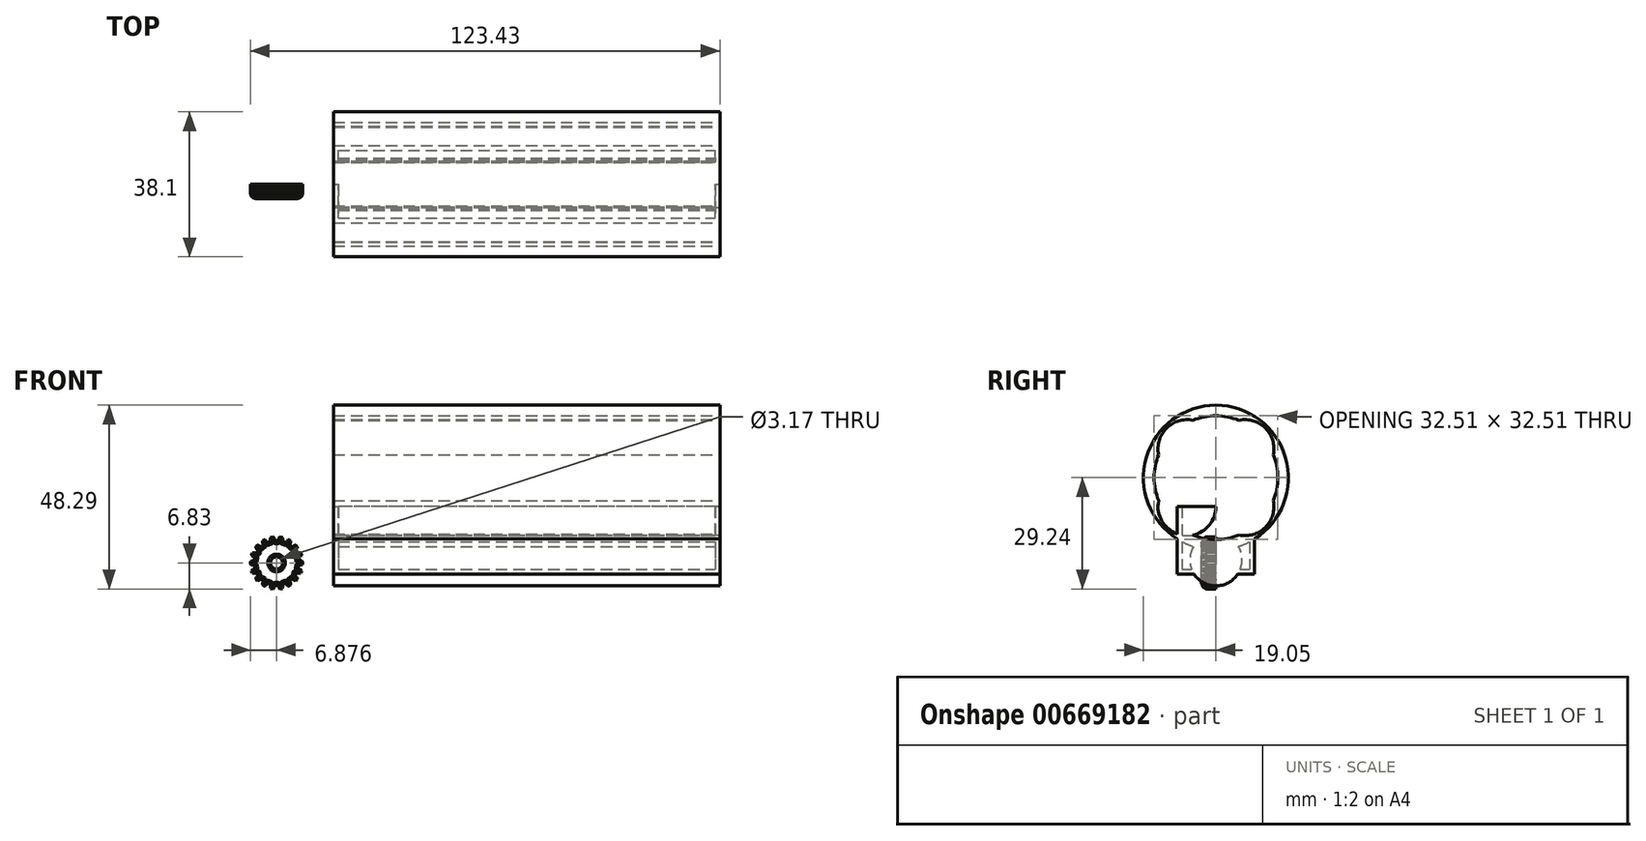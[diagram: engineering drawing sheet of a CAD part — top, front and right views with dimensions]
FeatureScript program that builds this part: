
annotation { "Feature Type Name" : "Feature", "Feature Type Description" : "" }
export const myFeature = defineFeature(function(context is Context, id is Id, definition is map)
    precondition{}
    {
        {
            var Q0;
            Q0=qCreatedBy(makeId("Top.planeOp"),FACE);
            var sketch = newSketch(context, id + "F0", { "sketchPlane" : qUnion([Q0])});
            skLineSegment(sketch, "E0.bottom", {"start": v(50.8, 10.16) * mm, "end": v(-50.8, 10.16) * mm});
            skLineSegment(sketch, "E0.top", {"start": v(50.8, -10.16) * mm, "end": v(-50.8, -10.16) * mm});
            skLineSegment(sketch, "E0.left", {"start": v(50.8, 10.16) * mm, "end": v(50.8, -10.16) * mm});
            skLineSegment(sketch, "E0.right", {"start": v(-50.8, 10.16) * mm, "end": v(-50.8, -10.16) * mm});
            skPoint(sketch, "E0.middle", {"position": v(0, 0) * mm});
            skLineSegment(sketch, "E1.0", {"start": v(49.53, 8.9) * mm, "end": v(-49.53, 8.9) * mm});
            skLineSegment(sketch, "E1.1", {"start": v(49.53, 8.9) * mm, "end": v(49.53, -8.9) * mm});
            skLineSegment(sketch, "E1.2", {"start": v(49.53, -8.9) * mm, "end": v(-49.53, -8.9) * mm});
            skLineSegment(sketch, "E1.3", {"start": v(-49.53, 8.9) * mm, "end": v(-49.53, -8.9) * mm});
            skSolve(sketch);
        }
        {
            var Q0;
            Q0=makeQuery(id+"F0.imprint","IMPRINT",FACE,{"disambiguationData":[TD([[makeQuery(id+"F0.imprint","IMPRINT",EDGE,{"derivedFrom":sQuery(id+"F0.wireOp",EDGE,"E1.0")}),1.0]])]});
            var Q1;
            Q1=makeQuery(id+"F0.imprint","IMPRINT",FACE,{"disambiguationData":[TD([[makeQuery(id+"F0.imprint","IMPRINT",EDGE,{"derivedFrom":sQuery(id+"F0.wireOp",EDGE,"E0.bottom")}),1.0]])]});
            extrude(context, id + "F1", {"entities" : qUnion([Q0, Q1]), "depth" : 1.27 * mm, "offsetDistance" : 25.4 * mm});
        }
        {
            var Q0;
            Q0=makeQuery(id+"F0.imprint","IMPRINT",FACE,{"disambiguationData":[TD([[makeQuery(id+"F0.imprint","IMPRINT",EDGE,{"derivedFrom":sQuery(id+"F0.wireOp",EDGE,"E0.bottom")}),1.0]])]});
            extrude(context, id + "F2", {"entities" : qUnion([Q0]), "operationType" : NewBodyOperationType.ADD, "depth" : 17.78 * mm, "offsetDistance" : 25.4 * mm});
        }
        {
            var Q0;
            {var subQ0=sQuery(id+"F0.wireOp",EDGE,"E0.top");Q0=makeQuery(id+"F2.boolean.opBoolean","MERGE",FACE,{"derivedFrom":[makeQuery(id+"F1.opExtrude","SWEPT_FACE",FACE,{"disambiguationData":[OSD([subQ0])]}),makeQuery(id+"F2.opExtrude","SWEPT_FACE",FACE,{"disambiguationData":[OSD([subQ0])]})]});}
            var sketch = newSketch(context, id + "F3", { "sketchPlane" : qUnion([Q0])});
            skCircle(sketch, "E2", {"center": v(35.56, 3.81) * mm, "radius": 12.7 * mm});
            skLineSegment(sketch, "E3", {"start": v(0, 1.21) * mm, "end": v(0, 17.78) * mm, "construction": true});
            skCircle(sketch, "E4.MirrorC", {"center": v(-35.56, 3.81) * mm, "radius": 12.7 * mm});
            skSolve(sketch);
        }
        {
            var Q0;
            {var subQ0=sQuery(id+"F0.wireOp",EDGE,"E0.left");Q0=makeQuery(id+"F2.boolean.opBoolean","MERGE",FACE,{"derivedFrom":[makeQuery(id+"F1.opExtrude","SWEPT_FACE",FACE,{"disambiguationData":[OSD([subQ0])]}),makeQuery(id+"F2.opExtrude","SWEPT_FACE",FACE,{"disambiguationData":[OSD([subQ0])]})]});}
            var sketch = newSketch(context, id + "F4", { "sketchPlane" : qUnion([Q0])});
            skCircle(sketch, "E5", {"center": v(0, 25.4) * mm, "radius": 19.05 * mm});
            skPoint(sketch, "E5.centerSnap0", {"position": v(0, 0) * mm});
            skPoint(sketch, "E6", {"position": v(0, 17.78) * mm});
            skCircle(sketch, "E7", {"center": v(-7.62, 33.02) * mm, "radius": 7.62 * mm});
            skCircle(sketch, "E8", {"center": v(7.62, 33.02) * mm, "radius": 7.62 * mm});
            skCircle(sketch, "E9", {"center": v(7.62, 17.78) * mm, "radius": 7.62 * mm});
            skCircle(sketch, "E10", {"center": v(-7.62, 17.78) * mm, "radius": 7.62 * mm});
            skLineSegment(sketch, "E11", {"start": v(-7.62, 33.02) * mm, "end": v(7.62, 17.78) * mm, "construction": true});
            skLineSegment(sketch, "E12", {"start": v(7.62, 33.02) * mm, "end": v(-7.62, 17.78) * mm, "construction": true});
            skPoint(sketch, "E13.0", {"position": v(-10.16, 3.81) * mm});
            skCircle(sketch, "E14", {"center": v(0, 3.81) * mm, "radius": 6.86 * mm});
            skCircle(sketch, "E15", {"center": v(0, 25.4) * mm, "radius": 16.26 * mm});
            skSolve(sketch);
        }
        {
            var Q0;
            Q0 = qSketchRegion(id + "F4", true);
            extrude(context, id + "F5", {"entities" : qUnion([Q0]), "operationType" : NewBodyOperationType.ADD, "oppositeDirection" : true, "depth" : 101.6 * mm, "offsetDistance" : 25.4 * mm});
        }
        {
            var Q0;
            {var subQ0=sQuery(id+"F4.wireOp",EDGE,"E15");var subQ1=sQuery(id+"F4.wireOp",EDGE,"E9");var subQ2=makeQuery(id+"F4.imprint","INTERSECT",VERTEX,{"disambiguationData":[OD(1.0)],"derivedFrom":[subQ1,subQ0]});Q0=makeQuery(id+"F4.imprint","IMPRINT",FACE,{"disambiguationData":[TD([[makeQuery(id+"F4.imprint","IMPRINT",EDGE,{"disambiguationData":[TD([[subQ2,1.0]])],"derivedFrom":subQ1}),1.0]])]});}
            var Q1;
            {var subQ0=sQuery(id+"F4.wireOp",EDGE,"E15");var subQ1=sQuery(id+"F4.wireOp",EDGE,"E14");var subQ2=makeQuery(id+"F4.imprint","INTERSECT",VERTEX,{"disambiguationData":[OD(0.0)],"derivedFrom":[subQ1,subQ0]});Q1=makeQuery(id+"F4.imprint","IMPRINT",FACE,{"disambiguationData":[TD([[makeQuery(id+"F4.imprint","IMPRINT",EDGE,{"disambiguationData":[TD([[subQ2,-1.0]])],"derivedFrom":subQ1}),1.0]])]});}
            var Q2;
            {var subQ0=sQuery(id+"F4.wireOp",EDGE,"E15");var subQ1=sQuery(id+"F4.wireOp",EDGE,"E14");var subQ2=makeQuery(id+"F4.imprint","INTERSECT",VERTEX,{"disambiguationData":[OD(0.0)],"derivedFrom":[subQ1,subQ0]});Q2=makeQuery(id+"F4.imprint","IMPRINT",FACE,{"disambiguationData":[TD([[makeQuery(id+"F4.imprint","IMPRINT",EDGE,{"disambiguationData":[TD([[subQ2,-1.0]])],"derivedFrom":subQ1}),-1.0]])]});}
            var Q3;
            {var subQ0=sQuery(id+"F4.wireOp",EDGE,"E15");var subQ1=sQuery(id+"F4.wireOp",EDGE,"E10");var subQ2=makeQuery(id+"F4.imprint","INTERSECT",VERTEX,{"disambiguationData":[OD(1.0)],"derivedFrom":[subQ1,subQ0]});Q3=makeQuery(id+"F4.imprint","IMPRINT",FACE,{"disambiguationData":[TD([[makeQuery(id+"F4.imprint","IMPRINT",EDGE,{"disambiguationData":[TD([[subQ2,-1.0]])],"derivedFrom":subQ1}),1.0]])]});}
            var Q4;
            {var subQ0=sQuery(id+"F4.wireOp",EDGE,"E15");var subQ1=sQuery(id+"F4.wireOp",EDGE,"E9");var subQ2=makeQuery(id+"F4.imprint","INTERSECT",VERTEX,{"disambiguationData":[OD(1.0)],"derivedFrom":[subQ1,subQ0]});Q4=makeQuery(id+"F4.imprint","IMPRINT",FACE,{"disambiguationData":[TD([[makeQuery(id+"F4.imprint","IMPRINT",EDGE,{"disambiguationData":[TD([[subQ2,-1.0]])],"derivedFrom":subQ1}),1.0]])]});}
            var Q5;
            {var subQ0=sQuery(id+"F4.wireOp",EDGE,"E15");var subQ1=sQuery(id+"F4.wireOp",EDGE,"E10");var subQ2=makeQuery(id+"F4.imprint","INTERSECT",VERTEX,{"disambiguationData":[OD(1.0)],"derivedFrom":[subQ1,subQ0]});Q5=makeQuery(id+"F4.imprint","IMPRINT",FACE,{"disambiguationData":[TD([[makeQuery(id+"F4.imprint","IMPRINT",EDGE,{"disambiguationData":[TD([[subQ2,1.0]])],"derivedFrom":subQ1}),1.0]])]});}
            extrude(context, id + "F6", {"entities" : qUnion([Q0, Q1, Q2, Q3, Q4, Q5]), "operationType" : NewBodyOperationType.REMOVE, "oppositeDirection" : true, "depth" : 101.6 * mm, "offsetDistance" : 25.4 * mm});
        }
        {
            var Q0;
            Q0=qCreatedBy(makeId("Front.planeOp"),FACE);
            var sketch = newSketch(context, id + "F7", { "sketchPlane" : qUnion([Q0])});
            skLineSegment(sketch, "E16", {"start": v(-59.99, 3.75) * mm, "end": v(-59.95, 3.68) * mm});
            skLineSegment(sketch, "E17", {"start": v(-59.95, 3.68) * mm, "end": v(-59.92, 3.66) * mm});
            skLineSegment(sketch, "E18", {"start": v(-59.92, 3.66) * mm, "end": v(-59.9, 3.64) * mm});
            skLineSegment(sketch, "E19", {"start": v(-59.9, 3.64) * mm, "end": v(-59.84, 3.62) * mm});
            skLineSegment(sketch, "E20", {"start": v(-59.84, 3.62) * mm, "end": v(-59.78, 3.6) * mm});
            skLineSegment(sketch, "E21", {"start": v(-59.78, 3.6) * mm, "end": v(-59.73, 3.6) * mm});
            skLineSegment(sketch, "E22", {"start": v(-59.73, 3.6) * mm, "end": v(-59.62, 3.58) * mm});
            skLineSegment(sketch, "E23", {"start": v(-59.62, 3.58) * mm, "end": v(-59.51, 3.56) * mm});
            skLineSegment(sketch, "E24", {"start": v(-59.51, 3.56) * mm, "end": v(-59.4, 3.54) * mm});
            skLineSegment(sketch, "E25", {"start": v(-59.4, 3.54) * mm, "end": v(-59.3, 3.5) * mm});
            skLineSegment(sketch, "E26", {"start": v(-59.3, 3.5) * mm, "end": v(-59.18, 3.46) * mm});
            skLineSegment(sketch, "E27", {"start": v(-59.18, 3.46) * mm, "end": v(-59.07, 3.42) * mm});
            skLineSegment(sketch, "E28", {"start": v(-59.07, 3.42) * mm, "end": v(-58.96, 3.37) * mm});
            skLineSegment(sketch, "E29", {"start": v(-58.96, 3.37) * mm, "end": v(-58.88, 3.33) * mm});
            skLineSegment(sketch, "E30", {"start": v(-58.88, 3.33) * mm, "end": v(-58.88, 2.65) * mm});
            skLineSegment(sketch, "E31", {"start": v(-58.88, 2.65) * mm, "end": v(-58.96, 2.61) * mm});
            skLineSegment(sketch, "E32", {"start": v(-58.96, 2.61) * mm, "end": v(-59.07, 2.56) * mm});
            skLineSegment(sketch, "E33", {"start": v(-59.07, 2.56) * mm, "end": v(-59.18, 2.52) * mm});
            skLineSegment(sketch, "E34", {"start": v(-59.18, 2.52) * mm, "end": v(-59.3, 2.48) * mm});
            skLineSegment(sketch, "E35", {"start": v(-59.3, 2.48) * mm, "end": v(-59.4, 2.44) * mm});
            skLineSegment(sketch, "E36", {"start": v(-59.4, 2.44) * mm, "end": v(-59.51, 2.42) * mm});
            skLineSegment(sketch, "E37", {"start": v(-59.51, 2.42) * mm, "end": v(-59.62, 2.4) * mm});
            skLineSegment(sketch, "E38", {"start": v(-59.62, 2.4) * mm, "end": v(-59.73, 2.38) * mm});
            skLineSegment(sketch, "E39", {"start": v(-59.73, 2.38) * mm, "end": v(-59.78, 2.38) * mm});
            skLineSegment(sketch, "E40", {"start": v(-59.78, 2.38) * mm, "end": v(-59.84, 2.36) * mm});
            skLineSegment(sketch, "E41", {"start": v(-59.84, 2.36) * mm, "end": v(-59.9, 2.34) * mm});
            skLineSegment(sketch, "E42", {"start": v(-59.9, 2.34) * mm, "end": v(-59.92, 2.33) * mm});
            skLineSegment(sketch, "E43", {"start": v(-59.92, 2.33) * mm, "end": v(-59.95, 2.3) * mm});
            skLineSegment(sketch, "E44", {"start": v(-59.95, 2.3) * mm, "end": v(-59.99, 2.23) * mm});
            skLineSegment(sketch, "E45", {"start": v(-59.99, 2.23) * mm, "end": v(-60.07, 1.73) * mm});
            skLineSegment(sketch, "E46", {"start": v(-60.07, 1.73) * mm, "end": v(-60.06, 1.65) * mm});
            skLineSegment(sketch, "E47", {"start": v(-60.06, 1.65) * mm, "end": v(-60.05, 1.62) * mm});
            skLineSegment(sketch, "E48", {"start": v(-60.05, 1.62) * mm, "end": v(-60.02, 1.6) * mm});
            skLineSegment(sketch, "E49", {"start": v(-60.02, 1.6) * mm, "end": v(-59.98, 1.56) * mm});
            skLineSegment(sketch, "E50", {"start": v(-59.98, 1.56) * mm, "end": v(-59.93, 1.52) * mm});
            skLineSegment(sketch, "E51", {"start": v(-59.93, 1.52) * mm, "end": v(-59.88, 1.5) * mm});
            skLineSegment(sketch, "E52", {"start": v(-59.88, 1.5) * mm, "end": v(-59.79, 1.45) * mm});
            skLineSegment(sketch, "E53", {"start": v(-59.79, 1.45) * mm, "end": v(-59.7, 1.4) * mm});
            skLineSegment(sketch, "E54", {"start": v(-59.7, 1.4) * mm, "end": v(-59.6, 1.33) * mm});
            skLineSegment(sketch, "E55", {"start": v(-59.6, 1.33) * mm, "end": v(-59.5, 1.26) * mm});
            skLineSegment(sketch, "E56", {"start": v(-59.5, 1.26) * mm, "end": v(-59.42, 1.19) * mm});
            skLineSegment(sketch, "E57", {"start": v(-59.42, 1.19) * mm, "end": v(-59.33, 1.1) * mm});
            skLineSegment(sketch, "E58", {"start": v(-59.33, 1.1) * mm, "end": v(-59.24, 1.02) * mm});
            skLineSegment(sketch, "E59", {"start": v(-59.24, 1.02) * mm, "end": v(-59.18, 0.96) * mm});
            skLineSegment(sketch, "E60", {"start": v(-59.18, 0.96) * mm, "end": v(-59.41, 0.32) * mm});
            skLineSegment(sketch, "E61", {"start": v(-59.41, 0.32) * mm, "end": v(-59.5, 0.31) * mm});
            skLineSegment(sketch, "E62", {"start": v(-59.5, 0.31) * mm, "end": v(-59.62, 0.3) * mm});
            skLineSegment(sketch, "E63", {"start": v(-59.62, 0.3) * mm, "end": v(-59.74, 0.3) * mm});
            skLineSegment(sketch, "E64", {"start": v(-59.74, 0.3) * mm, "end": v(-59.86, 0.3) * mm});
            skLineSegment(sketch, "E65", {"start": v(-59.86, 0.3) * mm, "end": v(-59.97, 0.3) * mm});
            skLineSegment(sketch, "E66", {"start": v(-59.97, 0.3) * mm, "end": v(-60.08, 0.32) * mm});
            skLineSegment(sketch, "E67", {"start": v(-60.08, 0.32) * mm, "end": v(-60.2, 0.33) * mm});
            skLineSegment(sketch, "E68", {"start": v(-60.2, 0.33) * mm, "end": v(-60.3, 0.36) * mm});
            skLineSegment(sketch, "E69", {"start": v(-60.3, 0.36) * mm, "end": v(-60.35, 0.37) * mm});
            skLineSegment(sketch, "E70", {"start": v(-60.35, 0.37) * mm, "end": v(-60.4, 0.38) * mm});
            skLineSegment(sketch, "E71", {"start": v(-60.4, 0.38) * mm, "end": v(-60.47, 0.38) * mm});
            skLineSegment(sketch, "E72", {"start": v(-60.47, 0.38) * mm, "end": v(-60.5, 0.37) * mm});
            skLineSegment(sketch, "E73", {"start": v(-60.5, 0.37) * mm, "end": v(-60.54, 0.36) * mm});
            skLineSegment(sketch, "E74", {"start": v(-60.54, 0.36) * mm, "end": v(-60.6, 0.3) * mm});
            skLineSegment(sketch, "E75", {"start": v(-60.6, 0.3) * mm, "end": v(-60.85, -0.14) * mm});
            skLineSegment(sketch, "E76", {"start": v(-60.85, -0.14) * mm, "end": v(-60.86, -0.21) * mm});
            skLineSegment(sketch, "E77", {"start": v(-60.86, -0.21) * mm, "end": v(-60.86, -0.25) * mm});
            skLineSegment(sketch, "E78", {"start": v(-60.86, -0.25) * mm, "end": v(-60.85, -0.28) * mm});
            skLineSegment(sketch, "E79", {"start": v(-60.85, -0.28) * mm, "end": v(-60.82, -0.33) * mm});
            skLineSegment(sketch, "E80", {"start": v(-60.82, -0.33) * mm, "end": v(-60.79, -0.38) * mm});
            skLineSegment(sketch, "E81", {"start": v(-60.79, -0.38) * mm, "end": v(-60.75, -0.42) * mm});
            skLineSegment(sketch, "E82", {"start": v(-60.75, -0.42) * mm, "end": v(-60.67, -0.5) * mm});
            skLineSegment(sketch, "E83", {"start": v(-60.67, -0.5) * mm, "end": v(-60.6, -0.58) * mm});
            skLineSegment(sketch, "E84", {"start": v(-60.6, -0.58) * mm, "end": v(-60.54, -0.68) * mm});
            skLineSegment(sketch, "E85", {"start": v(-60.54, -0.68) * mm, "end": v(-60.47, -0.77) * mm});
            skLineSegment(sketch, "E86", {"start": v(-60.47, -0.77) * mm, "end": v(-60.42, -0.87) * mm});
            skLineSegment(sketch, "E87", {"start": v(-60.42, -0.87) * mm, "end": v(-60.36, -0.98) * mm});
            skLineSegment(sketch, "E88", {"start": v(-60.36, -0.98) * mm, "end": v(-60.3, -1.09) * mm});
            skLineSegment(sketch, "E89", {"start": v(-60.3, -1.09) * mm, "end": v(-60.27, -1.17) * mm});
            skLineSegment(sketch, "E90", {"start": v(-60.27, -1.17) * mm, "end": v(-60.7, -1.69) * mm});
            skLineSegment(sketch, "E91", {"start": v(-60.7, -1.69) * mm, "end": v(-60.8, -1.67) * mm});
            skLineSegment(sketch, "E92", {"start": v(-60.8, -1.67) * mm, "end": v(-60.91, -1.63) * mm});
            skLineSegment(sketch, "E93", {"start": v(-60.91, -1.63) * mm, "end": v(-61.02, -1.6) * mm});
            skLineSegment(sketch, "E94", {"start": v(-61.02, -1.6) * mm, "end": v(-61.13, -1.56) * mm});
            skLineSegment(sketch, "E95", {"start": v(-61.13, -1.56) * mm, "end": v(-61.24, -1.51) * mm});
            skLineSegment(sketch, "E96", {"start": v(-61.24, -1.51) * mm, "end": v(-61.34, -1.46) * mm});
            skLineSegment(sketch, "E97", {"start": v(-61.34, -1.46) * mm, "end": v(-61.44, -1.4) * mm});
            skLineSegment(sketch, "E98", {"start": v(-61.44, -1.4) * mm, "end": v(-61.53, -1.35) * mm});
            skLineSegment(sketch, "E99", {"start": v(-61.53, -1.35) * mm, "end": v(-61.57, -1.32) * mm});
            skLineSegment(sketch, "E100", {"start": v(-61.57, -1.32) * mm, "end": v(-61.62, -1.3) * mm});
            skLineSegment(sketch, "E101", {"start": v(-61.62, -1.3) * mm, "end": v(-61.68, -1.27) * mm});
            skLineSegment(sketch, "E102", {"start": v(-61.68, -1.27) * mm, "end": v(-61.71, -1.27) * mm});
            skLineSegment(sketch, "E103", {"start": v(-61.71, -1.27) * mm, "end": v(-61.75, -1.27) * mm});
            skLineSegment(sketch, "E104", {"start": v(-61.75, -1.27) * mm, "end": v(-61.82, -1.3) * mm});
            skLineSegment(sketch, "E105", {"start": v(-61.82, -1.3) * mm, "end": v(-62.21, -1.63) * mm});
            skLineSegment(sketch, "E106", {"start": v(-62.21, -1.63) * mm, "end": v(-62.26, -1.7) * mm});
            skLineSegment(sketch, "E107", {"start": v(-62.26, -1.7) * mm, "end": v(-62.26, -1.73) * mm});
            skLineSegment(sketch, "E108", {"start": v(-62.26, -1.73) * mm, "end": v(-62.26, -1.76) * mm});
            skLineSegment(sketch, "E109", {"start": v(-62.26, -1.76) * mm, "end": v(-62.25, -1.82) * mm});
            skLineSegment(sketch, "E110", {"start": v(-62.25, -1.82) * mm, "end": v(-62.24, -1.88) * mm});
            skLineSegment(sketch, "E111", {"start": v(-62.24, -1.88) * mm, "end": v(-62.21, -1.93) * mm});
            skLineSegment(sketch, "E112", {"start": v(-62.21, -1.93) * mm, "end": v(-62.17, -2.03) * mm});
            skLineSegment(sketch, "E113", {"start": v(-62.17, -2.03) * mm, "end": v(-62.14, -2.13) * mm});
            skLineSegment(sketch, "E114", {"start": v(-62.14, -2.13) * mm, "end": v(-62.1, -2.24) * mm});
            skLineSegment(sketch, "E115", {"start": v(-62.1, -2.24) * mm, "end": v(-62.08, -2.35) * mm});
            skLineSegment(sketch, "E116", {"start": v(-62.08, -2.35) * mm, "end": v(-62.06, -2.46) * mm});
            skLineSegment(sketch, "E117", {"start": v(-62.06, -2.46) * mm, "end": v(-62.04, -2.58) * mm});
            skLineSegment(sketch, "E118", {"start": v(-62.04, -2.58) * mm, "end": v(-62.03, -2.7) * mm});
            skLineSegment(sketch, "E119", {"start": v(-62.03, -2.7) * mm, "end": v(-62.02, -2.8) * mm});
            skLineSegment(sketch, "E120", {"start": v(-62.02, -2.8) * mm, "end": v(-62.61, -3.13) * mm});
            skLineSegment(sketch, "E121", {"start": v(-62.61, -3.13) * mm, "end": v(-62.69, -3.08) * mm});
            skLineSegment(sketch, "E122", {"start": v(-62.69, -3.08) * mm, "end": v(-62.78, -3.01) * mm});
            skLineSegment(sketch, "E123", {"start": v(-62.78, -3.01) * mm, "end": v(-62.88, -2.94) * mm});
            skLineSegment(sketch, "E124", {"start": v(-62.88, -2.94) * mm, "end": v(-62.97, -2.86) * mm});
            skLineSegment(sketch, "E125", {"start": v(-62.97, -2.86) * mm, "end": v(-63.05, -2.78) * mm});
            skLineSegment(sketch, "E126", {"start": v(-63.05, -2.78) * mm, "end": v(-63.13, -2.7) * mm});
            skLineSegment(sketch, "E127", {"start": v(-63.13, -2.7) * mm, "end": v(-63.2, -2.62) * mm});
            skLineSegment(sketch, "E128", {"start": v(-63.2, -2.62) * mm, "end": v(-63.27, -2.53) * mm});
            skLineSegment(sketch, "E129", {"start": v(-63.27, -2.53) * mm, "end": v(-63.3, -2.49) * mm});
            skLineSegment(sketch, "E130", {"start": v(-63.3, -2.49) * mm, "end": v(-63.34, -2.45) * mm});
            skLineSegment(sketch, "E131", {"start": v(-63.34, -2.45) * mm, "end": v(-63.38, -2.41) * mm});
            skLineSegment(sketch, "E132", {"start": v(-63.38, -2.41) * mm, "end": v(-63.41, -2.4) * mm});
            skLineSegment(sketch, "E133", {"start": v(-63.41, -2.4) * mm, "end": v(-63.45, -2.38) * mm});
            skLineSegment(sketch, "E134", {"start": v(-63.45, -2.38) * mm, "end": v(-63.53, -2.38) * mm});
            skLineSegment(sketch, "E135", {"start": v(-63.53, -2.38) * mm, "end": v(-64, -2.56) * mm});
            skLineSegment(sketch, "E136", {"start": v(-64, -2.56) * mm, "end": v(-64.07, -2.6) * mm});
            skLineSegment(sketch, "E137", {"start": v(-64.07, -2.6) * mm, "end": v(-64.09, -2.64) * mm});
            skLineSegment(sketch, "E138", {"start": v(-64.09, -2.64) * mm, "end": v(-64.1, -2.67) * mm});
            skLineSegment(sketch, "E139", {"start": v(-64.1, -2.67) * mm, "end": v(-64.1, -2.73) * mm});
            skLineSegment(sketch, "E140", {"start": v(-64.1, -2.73) * mm, "end": v(-64.12, -2.79) * mm});
            skLineSegment(sketch, "E141", {"start": v(-64.12, -2.79) * mm, "end": v(-64.1, -2.84) * mm});
            skLineSegment(sketch, "E142", {"start": v(-64.1, -2.84) * mm, "end": v(-64.1, -2.95) * mm});
            skLineSegment(sketch, "E143", {"start": v(-64.1, -2.95) * mm, "end": v(-64.1, -3.06) * mm});
            skLineSegment(sketch, "E144", {"start": v(-64.1, -3.06) * mm, "end": v(-64.11, -3.17) * mm});
            skLineSegment(sketch, "E145", {"start": v(-64.11, -3.17) * mm, "end": v(-64.13, -3.29) * mm});
            skLineSegment(sketch, "E146", {"start": v(-64.13, -3.29) * mm, "end": v(-64.15, -3.4) * mm});
            skLineSegment(sketch, "E147", {"start": v(-64.15, -3.4) * mm, "end": v(-64.17, -3.52) * mm});
            skLineSegment(sketch, "E148", {"start": v(-64.17, -3.52) * mm, "end": v(-64.2, -3.63) * mm});
            skLineSegment(sketch, "E149", {"start": v(-64.2, -3.63) * mm, "end": v(-64.23, -3.72) * mm});
            skLineSegment(sketch, "E150", {"start": v(-64.23, -3.72) * mm, "end": v(-64.9, -3.84) * mm});
            skLineSegment(sketch, "E151", {"start": v(-64.9, -3.84) * mm, "end": v(-64.95, -3.76) * mm});
            skLineSegment(sketch, "E152", {"start": v(-64.95, -3.76) * mm, "end": v(-65.02, -3.66) * mm});
            skLineSegment(sketch, "E153", {"start": v(-65.02, -3.66) * mm, "end": v(-65.08, -3.56) * mm});
            skLineSegment(sketch, "E154", {"start": v(-65.08, -3.56) * mm, "end": v(-65.14, -3.46) * mm});
            skLineSegment(sketch, "E155", {"start": v(-65.14, -3.46) * mm, "end": v(-65.19, -3.36) * mm});
            skLineSegment(sketch, "E156", {"start": v(-65.19, -3.36) * mm, "end": v(-65.24, -3.26) * mm});
            skLineSegment(sketch, "E157", {"start": v(-65.24, -3.26) * mm, "end": v(-65.27, -3.15) * mm});
            skLineSegment(sketch, "E158", {"start": v(-65.27, -3.15) * mm, "end": v(-65.3, -3.05) * mm});
            skLineSegment(sketch, "E159", {"start": v(-65.3, -3.05) * mm, "end": v(-65.32, -3) * mm});
            skLineSegment(sketch, "E160", {"start": v(-65.32, -3) * mm, "end": v(-65.34, -2.95) * mm});
            skLineSegment(sketch, "E161", {"start": v(-65.34, -2.95) * mm, "end": v(-65.37, -2.9) * mm});
            skLineSegment(sketch, "E162", {"start": v(-65.37, -2.9) * mm, "end": v(-65.4, -2.87) * mm});
            skLineSegment(sketch, "E163", {"start": v(-65.4, -2.87) * mm, "end": v(-65.43, -2.85) * mm});
            skLineSegment(sketch, "E164", {"start": v(-65.43, -2.85) * mm, "end": v(-65.5, -2.82) * mm});
            skLineSegment(sketch, "E165", {"start": v(-65.5, -2.82) * mm, "end": v(-66, -2.82) * mm});
            skLineSegment(sketch, "E166", {"start": v(-66, -2.82) * mm, "end": v(-66.08, -2.85) * mm});
            skLineSegment(sketch, "E167", {"start": v(-66.08, -2.85) * mm, "end": v(-66.11, -2.87) * mm});
            skLineSegment(sketch, "E168", {"start": v(-66.11, -2.87) * mm, "end": v(-66.13, -2.9) * mm});
            skLineSegment(sketch, "E169", {"start": v(-66.13, -2.9) * mm, "end": v(-66.16, -2.95) * mm});
            skLineSegment(sketch, "E170", {"start": v(-66.16, -2.95) * mm, "end": v(-66.2, -3) * mm});
            skLineSegment(sketch, "E171", {"start": v(-66.2, -3) * mm, "end": v(-66.2, -3.05) * mm});
            skLineSegment(sketch, "E172", {"start": v(-66.2, -3.05) * mm, "end": v(-66.23, -3.15) * mm});
            skLineSegment(sketch, "E173", {"start": v(-66.23, -3.15) * mm, "end": v(-66.27, -3.26) * mm});
            skLineSegment(sketch, "E174", {"start": v(-66.27, -3.26) * mm, "end": v(-66.32, -3.36) * mm});
            skLineSegment(sketch, "E175", {"start": v(-66.32, -3.36) * mm, "end": v(-66.37, -3.46) * mm});
            skLineSegment(sketch, "E176", {"start": v(-66.37, -3.46) * mm, "end": v(-66.43, -3.56) * mm});
            skLineSegment(sketch, "E177", {"start": v(-66.43, -3.56) * mm, "end": v(-66.5, -3.66) * mm});
            skLineSegment(sketch, "E178", {"start": v(-66.5, -3.66) * mm, "end": v(-66.56, -3.76) * mm});
            skLineSegment(sketch, "E179", {"start": v(-66.56, -3.76) * mm, "end": v(-66.62, -3.84) * mm});
            skLineSegment(sketch, "E180", {"start": v(-66.62, -3.84) * mm, "end": v(-67.28, -3.72) * mm});
            skLineSegment(sketch, "E181", {"start": v(-67.28, -3.72) * mm, "end": v(-67.3, -3.63) * mm});
            skLineSegment(sketch, "E182", {"start": v(-67.3, -3.63) * mm, "end": v(-67.34, -3.52) * mm});
            skLineSegment(sketch, "E183", {"start": v(-67.34, -3.52) * mm, "end": v(-67.36, -3.4) * mm});
            skLineSegment(sketch, "E184", {"start": v(-67.36, -3.4) * mm, "end": v(-67.38, -3.29) * mm});
            skLineSegment(sketch, "E185", {"start": v(-67.38, -3.29) * mm, "end": v(-67.4, -3.17) * mm});
            skLineSegment(sketch, "E186", {"start": v(-67.4, -3.17) * mm, "end": v(-67.4, -3.06) * mm});
            skLineSegment(sketch, "E187", {"start": v(-67.4, -3.06) * mm, "end": v(-67.4, -2.95) * mm});
            skLineSegment(sketch, "E188", {"start": v(-67.4, -2.95) * mm, "end": v(-67.4, -2.84) * mm});
            skLineSegment(sketch, "E189", {"start": v(-67.4, -2.84) * mm, "end": v(-67.4, -2.79) * mm});
            skLineSegment(sketch, "E190", {"start": v(-67.4, -2.79) * mm, "end": v(-67.4, -2.73) * mm});
            skLineSegment(sketch, "E191", {"start": v(-67.4, -2.73) * mm, "end": v(-67.41, -2.67) * mm});
            skLineSegment(sketch, "E192", {"start": v(-67.41, -2.67) * mm, "end": v(-67.42, -2.64) * mm});
            skLineSegment(sketch, "E193", {"start": v(-67.42, -2.64) * mm, "end": v(-67.44, -2.6) * mm});
            skLineSegment(sketch, "E194", {"start": v(-67.44, -2.6) * mm, "end": v(-67.5, -2.56) * mm});
            skLineSegment(sketch, "E195", {"start": v(-67.5, -2.56) * mm, "end": v(-67.98, -2.38) * mm});
            skLineSegment(sketch, "E196", {"start": v(-67.98, -2.38) * mm, "end": v(-68.06, -2.38) * mm});
            skLineSegment(sketch, "E197", {"start": v(-68.06, -2.38) * mm, "end": v(-68.1, -2.4) * mm});
            skLineSegment(sketch, "E198", {"start": v(-68.1, -2.4) * mm, "end": v(-68.12, -2.41) * mm});
            skLineSegment(sketch, "E199", {"start": v(-68.12, -2.41) * mm, "end": v(-68.17, -2.45) * mm});
            skLineSegment(sketch, "E200", {"start": v(-68.17, -2.45) * mm, "end": v(-68.21, -2.49) * mm});
            skLineSegment(sketch, "E201", {"start": v(-68.21, -2.49) * mm, "end": v(-68.24, -2.53) * mm});
            skLineSegment(sketch, "E202", {"start": v(-68.24, -2.53) * mm, "end": v(-68.3, -2.62) * mm});
            skLineSegment(sketch, "E203", {"start": v(-68.3, -2.62) * mm, "end": v(-68.38, -2.7) * mm});
            skLineSegment(sketch, "E204", {"start": v(-68.38, -2.7) * mm, "end": v(-68.46, -2.78) * mm});
            skLineSegment(sketch, "E205", {"start": v(-68.46, -2.78) * mm, "end": v(-68.54, -2.86) * mm});
            skLineSegment(sketch, "E206", {"start": v(-68.54, -2.86) * mm, "end": v(-68.63, -2.94) * mm});
            skLineSegment(sketch, "E207", {"start": v(-68.63, -2.94) * mm, "end": v(-68.72, -3.01) * mm});
            skLineSegment(sketch, "E208", {"start": v(-68.72, -3.01) * mm, "end": v(-68.82, -3.08) * mm});
            skLineSegment(sketch, "E209", {"start": v(-68.82, -3.08) * mm, "end": v(-68.9, -3.13) * mm});
            skLineSegment(sketch, "E210", {"start": v(-68.9, -3.13) * mm, "end": v(-69.48, -2.8) * mm});
            skLineSegment(sketch, "E211", {"start": v(-69.48, -2.8) * mm, "end": v(-69.48, -2.7) * mm});
            skLineSegment(sketch, "E212", {"start": v(-69.48, -2.7) * mm, "end": v(-69.47, -2.58) * mm});
            skLineSegment(sketch, "E213", {"start": v(-69.47, -2.58) * mm, "end": v(-69.45, -2.46) * mm});
            skLineSegment(sketch, "E214", {"start": v(-69.45, -2.46) * mm, "end": v(-69.43, -2.35) * mm});
            skLineSegment(sketch, "E215", {"start": v(-69.43, -2.35) * mm, "end": v(-69.4, -2.24) * mm});
            skLineSegment(sketch, "E216", {"start": v(-69.4, -2.24) * mm, "end": v(-69.37, -2.13) * mm});
            skLineSegment(sketch, "E217", {"start": v(-69.37, -2.13) * mm, "end": v(-69.34, -2.03) * mm});
            skLineSegment(sketch, "E218", {"start": v(-69.34, -2.03) * mm, "end": v(-69.3, -1.93) * mm});
            skLineSegment(sketch, "E219", {"start": v(-69.3, -1.93) * mm, "end": v(-69.27, -1.88) * mm});
            skLineSegment(sketch, "E220", {"start": v(-69.27, -1.88) * mm, "end": v(-69.26, -1.82) * mm});
            skLineSegment(sketch, "E221", {"start": v(-69.26, -1.82) * mm, "end": v(-69.25, -1.76) * mm});
            skLineSegment(sketch, "E222", {"start": v(-69.25, -1.76) * mm, "end": v(-69.25, -1.73) * mm});
            skLineSegment(sketch, "E223", {"start": v(-69.25, -1.73) * mm, "end": v(-69.25, -1.7) * mm});
            skLineSegment(sketch, "E224", {"start": v(-69.25, -1.7) * mm, "end": v(-69.3, -1.63) * mm});
            skLineSegment(sketch, "E225", {"start": v(-69.3, -1.63) * mm, "end": v(-69.69, -1.3) * mm});
            skLineSegment(sketch, "E226", {"start": v(-69.69, -1.3) * mm, "end": v(-69.76, -1.27) * mm});
            skLineSegment(sketch, "E227", {"start": v(-69.76, -1.27) * mm, "end": v(-69.8, -1.27) * mm});
            skLineSegment(sketch, "E228", {"start": v(-69.8, -1.27) * mm, "end": v(-69.83, -1.27) * mm});
            skLineSegment(sketch, "E229", {"start": v(-69.83, -1.27) * mm, "end": v(-69.89, -1.3) * mm});
            skLineSegment(sketch, "E230", {"start": v(-69.89, -1.3) * mm, "end": v(-69.94, -1.32) * mm});
            skLineSegment(sketch, "E231", {"start": v(-69.94, -1.32) * mm, "end": v(-69.98, -1.35) * mm});
            skLineSegment(sketch, "E232", {"start": v(-69.98, -1.35) * mm, "end": v(-70.07, -1.4) * mm});
            skLineSegment(sketch, "E233", {"start": v(-70.07, -1.4) * mm, "end": v(-70.17, -1.46) * mm});
            skLineSegment(sketch, "E234", {"start": v(-70.17, -1.46) * mm, "end": v(-70.27, -1.51) * mm});
            skLineSegment(sketch, "E235", {"start": v(-70.27, -1.51) * mm, "end": v(-70.38, -1.56) * mm});
            skLineSegment(sketch, "E236", {"start": v(-70.38, -1.56) * mm, "end": v(-70.49, -1.6) * mm});
            skLineSegment(sketch, "E237", {"start": v(-70.49, -1.6) * mm, "end": v(-70.6, -1.63) * mm});
            skLineSegment(sketch, "E238", {"start": v(-70.6, -1.63) * mm, "end": v(-70.71, -1.67) * mm});
            skLineSegment(sketch, "E239", {"start": v(-70.71, -1.67) * mm, "end": v(-70.8, -1.69) * mm});
            skLineSegment(sketch, "E240", {"start": v(-70.8, -1.69) * mm, "end": v(-71.24, -1.17) * mm});
            skLineSegment(sketch, "E241", {"start": v(-71.24, -1.17) * mm, "end": v(-71.2, -1.09) * mm});
            skLineSegment(sketch, "E242", {"start": v(-71.2, -1.09) * mm, "end": v(-71.15, -0.98) * mm});
            skLineSegment(sketch, "E243", {"start": v(-71.15, -0.98) * mm, "end": v(-71.1, -0.87) * mm});
            skLineSegment(sketch, "E244", {"start": v(-71.1, -0.87) * mm, "end": v(-71.03, -0.77) * mm});
            skLineSegment(sketch, "E245", {"start": v(-71.03, -0.77) * mm, "end": v(-70.97, -0.68) * mm});
            skLineSegment(sketch, "E246", {"start": v(-70.97, -0.68) * mm, "end": v(-70.9, -0.58) * mm});
            skLineSegment(sketch, "E247", {"start": v(-70.9, -0.58) * mm, "end": v(-70.84, -0.5) * mm});
            skLineSegment(sketch, "E248", {"start": v(-70.84, -0.5) * mm, "end": v(-70.76, -0.42) * mm});
            skLineSegment(sketch, "E249", {"start": v(-70.76, -0.42) * mm, "end": v(-70.72, -0.38) * mm});
            skLineSegment(sketch, "E250", {"start": v(-70.72, -0.38) * mm, "end": v(-70.7, -0.33) * mm});
            skLineSegment(sketch, "E251", {"start": v(-70.7, -0.33) * mm, "end": v(-70.66, -0.28) * mm});
            skLineSegment(sketch, "E252", {"start": v(-70.66, -0.28) * mm, "end": v(-70.65, -0.25) * mm});
            skLineSegment(sketch, "E253", {"start": v(-70.65, -0.25) * mm, "end": v(-70.64, -0.21) * mm});
            skLineSegment(sketch, "E254", {"start": v(-70.64, -0.21) * mm, "end": v(-70.66, -0.14) * mm});
            skLineSegment(sketch, "E255", {"start": v(-70.66, -0.14) * mm, "end": v(-70.92, 0.3) * mm});
            skLineSegment(sketch, "E256", {"start": v(-70.92, 0.3) * mm, "end": v(-70.97, 0.36) * mm});
            skLineSegment(sketch, "E257", {"start": v(-70.97, 0.36) * mm, "end": v(-71, 0.37) * mm});
            skLineSegment(sketch, "E258", {"start": v(-71, 0.37) * mm, "end": v(-71.04, 0.38) * mm});
            skLineSegment(sketch, "E259", {"start": v(-71.04, 0.38) * mm, "end": v(-71.1, 0.38) * mm});
            skLineSegment(sketch, "E260", {"start": v(-71.1, 0.38) * mm, "end": v(-71.16, 0.37) * mm});
            skLineSegment(sketch, "E261", {"start": v(-71.16, 0.37) * mm, "end": v(-71.21, 0.36) * mm});
            skLineSegment(sketch, "E262", {"start": v(-71.21, 0.36) * mm, "end": v(-71.32, 0.33) * mm});
            skLineSegment(sketch, "E263", {"start": v(-71.32, 0.33) * mm, "end": v(-71.43, 0.32) * mm});
            skLineSegment(sketch, "E264", {"start": v(-71.43, 0.32) * mm, "end": v(-71.54, 0.3) * mm});
            skLineSegment(sketch, "E265", {"start": v(-71.54, 0.3) * mm, "end": v(-71.65, 0.3) * mm});
            skLineSegment(sketch, "E266", {"start": v(-71.65, 0.3) * mm, "end": v(-71.77, 0.3) * mm});
            skLineSegment(sketch, "E267", {"start": v(-71.77, 0.3) * mm, "end": v(-71.89, 0.3) * mm});
            skLineSegment(sketch, "E268", {"start": v(-71.89, 0.3) * mm, "end": v(-72, 0.31) * mm});
            skLineSegment(sketch, "E269", {"start": v(-72, 0.31) * mm, "end": v(-72.1, 0.32) * mm});
            skLineSegment(sketch, "E270", {"start": v(-72.1, 0.32) * mm, "end": v(-72.33, 0.96) * mm});
            skLineSegment(sketch, "E271", {"start": v(-72.33, 0.96) * mm, "end": v(-72.27, 1.02) * mm});
            skLineSegment(sketch, "E272", {"start": v(-72.27, 1.02) * mm, "end": v(-72.18, 1.1) * mm});
            skLineSegment(sketch, "E273", {"start": v(-72.18, 1.1) * mm, "end": v(-72.1, 1.19) * mm});
            skLineSegment(sketch, "E274", {"start": v(-72.1, 1.19) * mm, "end": v(-72, 1.26) * mm});
            skLineSegment(sketch, "E275", {"start": v(-72, 1.26) * mm, "end": v(-71.91, 1.33) * mm});
            skLineSegment(sketch, "E276", {"start": v(-71.91, 1.33) * mm, "end": v(-71.82, 1.4) * mm});
            skLineSegment(sketch, "E277", {"start": v(-71.82, 1.4) * mm, "end": v(-71.72, 1.45) * mm});
            skLineSegment(sketch, "E278", {"start": v(-71.72, 1.45) * mm, "end": v(-71.63, 1.5) * mm});
            skLineSegment(sketch, "E279", {"start": v(-71.63, 1.5) * mm, "end": v(-71.58, 1.52) * mm});
            skLineSegment(sketch, "E280", {"start": v(-71.58, 1.52) * mm, "end": v(-71.53, 1.56) * mm});
            skLineSegment(sketch, "E281", {"start": v(-71.53, 1.56) * mm, "end": v(-71.48, 1.6) * mm});
            skLineSegment(sketch, "E282", {"start": v(-71.48, 1.6) * mm, "end": v(-71.46, 1.62) * mm});
            skLineSegment(sketch, "E283", {"start": v(-71.46, 1.62) * mm, "end": v(-71.44, 1.65) * mm});
            skLineSegment(sketch, "E284", {"start": v(-71.44, 1.65) * mm, "end": v(-71.43, 1.73) * mm});
            skLineSegment(sketch, "E285", {"start": v(-71.43, 1.73) * mm, "end": v(-71.52, 2.23) * mm});
            skLineSegment(sketch, "E286", {"start": v(-71.52, 2.23) * mm, "end": v(-71.56, 2.3) * mm});
            skLineSegment(sketch, "E287", {"start": v(-71.56, 2.3) * mm, "end": v(-71.59, 2.33) * mm});
            skLineSegment(sketch, "E288", {"start": v(-71.59, 2.33) * mm, "end": v(-71.62, 2.34) * mm});
            skLineSegment(sketch, "E289", {"start": v(-71.62, 2.34) * mm, "end": v(-71.67, 2.36) * mm});
            skLineSegment(sketch, "E290", {"start": v(-71.67, 2.36) * mm, "end": v(-71.73, 2.38) * mm});
            skLineSegment(sketch, "E291", {"start": v(-71.73, 2.38) * mm, "end": v(-71.78, 2.38) * mm});
            skLineSegment(sketch, "E292", {"start": v(-71.78, 2.38) * mm, "end": v(-71.89, 2.4) * mm});
            skLineSegment(sketch, "E293", {"start": v(-71.89, 2.4) * mm, "end": v(-72, 2.42) * mm});
            skLineSegment(sketch, "E294", {"start": v(-72, 2.42) * mm, "end": v(-72.1, 2.44) * mm});
            skLineSegment(sketch, "E295", {"start": v(-72.1, 2.44) * mm, "end": v(-72.22, 2.48) * mm});
            skLineSegment(sketch, "E296", {"start": v(-72.22, 2.48) * mm, "end": v(-72.33, 2.52) * mm});
            skLineSegment(sketch, "E297", {"start": v(-72.33, 2.52) * mm, "end": v(-72.44, 2.56) * mm});
            skLineSegment(sketch, "E298", {"start": v(-72.44, 2.56) * mm, "end": v(-72.55, 2.61) * mm});
            skLineSegment(sketch, "E299", {"start": v(-72.55, 2.61) * mm, "end": v(-72.63, 2.65) * mm});
            skLineSegment(sketch, "E300", {"start": v(-72.63, 2.65) * mm, "end": v(-72.63, 3.33) * mm});
            skLineSegment(sketch, "E301", {"start": v(-72.63, 3.33) * mm, "end": v(-72.55, 3.37) * mm});
            skLineSegment(sketch, "E302", {"start": v(-72.55, 3.37) * mm, "end": v(-72.44, 3.42) * mm});
            skLineSegment(sketch, "E303", {"start": v(-72.44, 3.42) * mm, "end": v(-72.33, 3.46) * mm});
            skLineSegment(sketch, "E304", {"start": v(-72.33, 3.46) * mm, "end": v(-72.22, 3.5) * mm});
            skLineSegment(sketch, "E305", {"start": v(-72.22, 3.5) * mm, "end": v(-72.1, 3.54) * mm});
            skLineSegment(sketch, "E306", {"start": v(-72.1, 3.54) * mm, "end": v(-72, 3.56) * mm});
            skLineSegment(sketch, "E307", {"start": v(-72, 3.56) * mm, "end": v(-71.89, 3.58) * mm});
            skLineSegment(sketch, "E308", {"start": v(-71.89, 3.58) * mm, "end": v(-71.78, 3.6) * mm});
            skLineSegment(sketch, "E309", {"start": v(-71.78, 3.6) * mm, "end": v(-71.73, 3.6) * mm});
            skLineSegment(sketch, "E310", {"start": v(-71.73, 3.6) * mm, "end": v(-71.67, 3.62) * mm});
            skLineSegment(sketch, "E311", {"start": v(-71.67, 3.62) * mm, "end": v(-71.62, 3.64) * mm});
            skLineSegment(sketch, "E312", {"start": v(-71.62, 3.64) * mm, "end": v(-71.59, 3.66) * mm});
            skLineSegment(sketch, "E313", {"start": v(-71.59, 3.66) * mm, "end": v(-71.56, 3.68) * mm});
            skLineSegment(sketch, "E314", {"start": v(-71.56, 3.68) * mm, "end": v(-71.52, 3.75) * mm});
            skLineSegment(sketch, "E315", {"start": v(-71.52, 3.75) * mm, "end": v(-71.43, 4.25) * mm});
            skLineSegment(sketch, "E316", {"start": v(-71.43, 4.25) * mm, "end": v(-71.44, 4.33) * mm});
            skLineSegment(sketch, "E317", {"start": v(-71.44, 4.33) * mm, "end": v(-71.46, 4.36) * mm});
            skLineSegment(sketch, "E318", {"start": v(-71.46, 4.36) * mm, "end": v(-71.48, 4.39) * mm});
            skLineSegment(sketch, "E319", {"start": v(-71.48, 4.39) * mm, "end": v(-71.53, 4.43) * mm});
            skLineSegment(sketch, "E320", {"start": v(-71.53, 4.43) * mm, "end": v(-71.58, 4.46) * mm});
            skLineSegment(sketch, "E321", {"start": v(-71.58, 4.46) * mm, "end": v(-71.63, 4.48) * mm});
            skLineSegment(sketch, "E322", {"start": v(-71.63, 4.48) * mm, "end": v(-71.72, 4.53) * mm});
            skLineSegment(sketch, "E323", {"start": v(-71.72, 4.53) * mm, "end": v(-71.82, 4.59) * mm});
            skLineSegment(sketch, "E324", {"start": v(-71.82, 4.59) * mm, "end": v(-71.91, 4.65) * mm});
            skLineSegment(sketch, "E325", {"start": v(-71.91, 4.65) * mm, "end": v(-72, 4.72) * mm});
            skLineSegment(sketch, "E326", {"start": v(-72, 4.72) * mm, "end": v(-72.1, 4.8) * mm});
            skLineSegment(sketch, "E327", {"start": v(-72.1, 4.8) * mm, "end": v(-72.18, 4.87) * mm});
            skLineSegment(sketch, "E328", {"start": v(-72.18, 4.87) * mm, "end": v(-72.27, 4.96) * mm});
            skLineSegment(sketch, "E329", {"start": v(-72.27, 4.96) * mm, "end": v(-72.33, 5.02) * mm});
            skLineSegment(sketch, "E330", {"start": v(-72.33, 5.02) * mm, "end": v(-72.1, 5.66) * mm});
            skLineSegment(sketch, "E331", {"start": v(-72.1, 5.66) * mm, "end": v(-72, 5.67) * mm});
            skLineSegment(sketch, "E332", {"start": v(-72, 5.67) * mm, "end": v(-71.89, 5.68) * mm});
            skLineSegment(sketch, "E333", {"start": v(-71.89, 5.68) * mm, "end": v(-71.77, 5.68) * mm});
            skLineSegment(sketch, "E334", {"start": v(-71.77, 5.68) * mm, "end": v(-71.65, 5.68) * mm});
            skLineSegment(sketch, "E335", {"start": v(-71.65, 5.68) * mm, "end": v(-71.54, 5.68) * mm});
            skLineSegment(sketch, "E336", {"start": v(-71.54, 5.68) * mm, "end": v(-71.43, 5.66) * mm});
            skLineSegment(sketch, "E337", {"start": v(-71.43, 5.66) * mm, "end": v(-71.32, 5.65) * mm});
            skLineSegment(sketch, "E338", {"start": v(-71.32, 5.65) * mm, "end": v(-71.21, 5.62) * mm});
            skLineSegment(sketch, "E339", {"start": v(-71.21, 5.62) * mm, "end": v(-71.16, 5.6) * mm});
            skLineSegment(sketch, "E340", {"start": v(-71.16, 5.6) * mm, "end": v(-71.1, 5.6) * mm});
            skLineSegment(sketch, "E341", {"start": v(-71.1, 5.6) * mm, "end": v(-71.04, 5.6) * mm});
            skLineSegment(sketch, "E342", {"start": v(-71.04, 5.6) * mm, "end": v(-71, 5.61) * mm});
            skLineSegment(sketch, "E343", {"start": v(-71, 5.61) * mm, "end": v(-70.97, 5.62) * mm});
            skLineSegment(sketch, "E344", {"start": v(-70.97, 5.62) * mm, "end": v(-70.92, 5.68) * mm});
            skLineSegment(sketch, "E345", {"start": v(-70.92, 5.68) * mm, "end": v(-70.66, 6.12) * mm});
            skLineSegment(sketch, "E346", {"start": v(-70.66, 6.12) * mm, "end": v(-70.64, 6.2) * mm});
            skLineSegment(sketch, "E347", {"start": v(-70.64, 6.2) * mm, "end": v(-70.65, 6.23) * mm});
            skLineSegment(sketch, "E348", {"start": v(-70.65, 6.23) * mm, "end": v(-70.66, 6.26) * mm});
            skLineSegment(sketch, "E349", {"start": v(-70.66, 6.26) * mm, "end": v(-70.7, 6.31) * mm});
            skLineSegment(sketch, "E350", {"start": v(-70.7, 6.31) * mm, "end": v(-70.72, 6.36) * mm});
            skLineSegment(sketch, "E351", {"start": v(-70.72, 6.36) * mm, "end": v(-70.76, 6.4) * mm});
            skLineSegment(sketch, "E352", {"start": v(-70.76, 6.4) * mm, "end": v(-70.84, 6.48) * mm});
            skLineSegment(sketch, "E353", {"start": v(-70.84, 6.48) * mm, "end": v(-70.9, 6.56) * mm});
            skLineSegment(sketch, "E354", {"start": v(-70.9, 6.56) * mm, "end": v(-70.97, 6.66) * mm});
            skLineSegment(sketch, "E355", {"start": v(-70.97, 6.66) * mm, "end": v(-71.03, 6.75) * mm});
            skLineSegment(sketch, "E356", {"start": v(-71.03, 6.75) * mm, "end": v(-71.1, 6.85) * mm});
            skLineSegment(sketch, "E357", {"start": v(-71.1, 6.85) * mm, "end": v(-71.15, 6.96) * mm});
            skLineSegment(sketch, "E358", {"start": v(-71.15, 6.96) * mm, "end": v(-71.2, 7.07) * mm});
            skLineSegment(sketch, "E359", {"start": v(-71.2, 7.07) * mm, "end": v(-71.24, 7.15) * mm});
            skLineSegment(sketch, "E360", {"start": v(-71.24, 7.15) * mm, "end": v(-70.8, 7.67) * mm});
            skLineSegment(sketch, "E361", {"start": v(-70.8, 7.67) * mm, "end": v(-70.71, 7.65) * mm});
            skLineSegment(sketch, "E362", {"start": v(-70.71, 7.65) * mm, "end": v(-70.6, 7.61) * mm});
            skLineSegment(sketch, "E363", {"start": v(-70.6, 7.61) * mm, "end": v(-70.49, 7.58) * mm});
            skLineSegment(sketch, "E364", {"start": v(-70.49, 7.58) * mm, "end": v(-70.38, 7.54) * mm});
            skLineSegment(sketch, "E365", {"start": v(-70.38, 7.54) * mm, "end": v(-70.27, 7.5) * mm});
            skLineSegment(sketch, "E366", {"start": v(-70.27, 7.5) * mm, "end": v(-70.17, 7.44) * mm});
            skLineSegment(sketch, "E367", {"start": v(-70.17, 7.44) * mm, "end": v(-70.07, 7.39) * mm});
            skLineSegment(sketch, "E368", {"start": v(-70.07, 7.39) * mm, "end": v(-69.98, 7.33) * mm});
            skLineSegment(sketch, "E369", {"start": v(-69.98, 7.33) * mm, "end": v(-69.94, 7.3) * mm});
            skLineSegment(sketch, "E370", {"start": v(-69.94, 7.3) * mm, "end": v(-69.89, 7.27) * mm});
            skLineSegment(sketch, "E371", {"start": v(-69.89, 7.27) * mm, "end": v(-69.83, 7.26) * mm});
            skLineSegment(sketch, "E372", {"start": v(-69.83, 7.26) * mm, "end": v(-69.8, 7.25) * mm});
            skLineSegment(sketch, "E373", {"start": v(-69.8, 7.25) * mm, "end": v(-69.76, 7.25) * mm});
            skLineSegment(sketch, "E374", {"start": v(-69.76, 7.25) * mm, "end": v(-69.69, 7.28) * mm});
            skLineSegment(sketch, "E375", {"start": v(-69.69, 7.28) * mm, "end": v(-69.3, 7.6) * mm});
            skLineSegment(sketch, "E376", {"start": v(-69.3, 7.6) * mm, "end": v(-69.25, 7.67) * mm});
            skLineSegment(sketch, "E377", {"start": v(-69.25, 7.67) * mm, "end": v(-69.25, 7.7) * mm});
            skLineSegment(sketch, "E378", {"start": v(-69.25, 7.7) * mm, "end": v(-69.25, 7.74) * mm});
            skLineSegment(sketch, "E379", {"start": v(-69.25, 7.74) * mm, "end": v(-69.26, 7.8) * mm});
            skLineSegment(sketch, "E380", {"start": v(-69.26, 7.8) * mm, "end": v(-69.27, 7.86) * mm});
            skLineSegment(sketch, "E381", {"start": v(-69.27, 7.86) * mm, "end": v(-69.3, 7.9) * mm});
            skLineSegment(sketch, "E382", {"start": v(-69.3, 7.9) * mm, "end": v(-69.34, 8) * mm});
            skLineSegment(sketch, "E383", {"start": v(-69.34, 8) * mm, "end": v(-69.37, 8.11) * mm});
            skLineSegment(sketch, "E384", {"start": v(-69.37, 8.11) * mm, "end": v(-69.4, 8.22) * mm});
            skLineSegment(sketch, "E385", {"start": v(-69.4, 8.22) * mm, "end": v(-69.43, 8.33) * mm});
            skLineSegment(sketch, "E386", {"start": v(-69.43, 8.33) * mm, "end": v(-69.45, 8.45) * mm});
            skLineSegment(sketch, "E387", {"start": v(-69.45, 8.45) * mm, "end": v(-69.47, 8.56) * mm});
            skLineSegment(sketch, "E388", {"start": v(-69.47, 8.56) * mm, "end": v(-69.48, 8.68) * mm});
            skLineSegment(sketch, "E389", {"start": v(-69.48, 8.68) * mm, "end": v(-69.48, 8.77) * mm});
            skLineSegment(sketch, "E390", {"start": v(-69.48, 8.77) * mm, "end": v(-68.9, 9.11) * mm});
            skLineSegment(sketch, "E391", {"start": v(-68.9, 9.11) * mm, "end": v(-68.82, 9.06) * mm});
            skLineSegment(sketch, "E392", {"start": v(-68.82, 9.06) * mm, "end": v(-68.72, 9) * mm});
            skLineSegment(sketch, "E393", {"start": v(-68.72, 9) * mm, "end": v(-68.63, 8.92) * mm});
            skLineSegment(sketch, "E394", {"start": v(-68.63, 8.92) * mm, "end": v(-68.54, 8.84) * mm});
            skLineSegment(sketch, "E395", {"start": v(-68.54, 8.84) * mm, "end": v(-68.46, 8.77) * mm});
            skLineSegment(sketch, "E396", {"start": v(-68.46, 8.77) * mm, "end": v(-68.38, 8.68) * mm});
            skLineSegment(sketch, "E397", {"start": v(-68.38, 8.68) * mm, "end": v(-68.3, 8.6) * mm});
            skLineSegment(sketch, "E398", {"start": v(-68.3, 8.6) * mm, "end": v(-68.24, 8.51) * mm});
            skLineSegment(sketch, "E399", {"start": v(-68.24, 8.51) * mm, "end": v(-68.21, 8.47) * mm});
            skLineSegment(sketch, "E400", {"start": v(-68.21, 8.47) * mm, "end": v(-68.17, 8.43) * mm});
            skLineSegment(sketch, "E401", {"start": v(-68.17, 8.43) * mm, "end": v(-68.12, 8.4) * mm});
            skLineSegment(sketch, "E402", {"start": v(-68.12, 8.4) * mm, "end": v(-68.1, 8.38) * mm});
            skLineSegment(sketch, "E403", {"start": v(-68.1, 8.38) * mm, "end": v(-68.06, 8.36) * mm});
            skLineSegment(sketch, "E404", {"start": v(-68.06, 8.36) * mm, "end": v(-67.98, 8.37) * mm});
            skLineSegment(sketch, "E405", {"start": v(-67.98, 8.37) * mm, "end": v(-67.5, 8.54) * mm});
            skLineSegment(sketch, "E406", {"start": v(-67.5, 8.54) * mm, "end": v(-67.44, 8.59) * mm});
            skLineSegment(sketch, "E407", {"start": v(-67.44, 8.59) * mm, "end": v(-67.42, 8.62) * mm});
            skLineSegment(sketch, "E408", {"start": v(-67.42, 8.62) * mm, "end": v(-67.41, 8.65) * mm});
            skLineSegment(sketch, "E409", {"start": v(-67.41, 8.65) * mm, "end": v(-67.4, 8.7) * mm});
            skLineSegment(sketch, "E410", {"start": v(-67.4, 8.7) * mm, "end": v(-67.4, 8.77) * mm});
            skLineSegment(sketch, "E411", {"start": v(-67.4, 8.77) * mm, "end": v(-67.4, 8.82) * mm});
            skLineSegment(sketch, "E412", {"start": v(-67.4, 8.82) * mm, "end": v(-67.4, 8.93) * mm});
            skLineSegment(sketch, "E413", {"start": v(-67.4, 8.93) * mm, "end": v(-67.4, 9.04) * mm});
            skLineSegment(sketch, "E414", {"start": v(-67.4, 9.04) * mm, "end": v(-67.4, 9.15) * mm});
            skLineSegment(sketch, "E415", {"start": v(-67.4, 9.15) * mm, "end": v(-67.38, 9.27) * mm});
            skLineSegment(sketch, "E416", {"start": v(-67.38, 9.27) * mm, "end": v(-67.36, 9.38) * mm});
            skLineSegment(sketch, "E417", {"start": v(-67.36, 9.38) * mm, "end": v(-67.34, 9.5) * mm});
            skLineSegment(sketch, "E418", {"start": v(-67.34, 9.5) * mm, "end": v(-67.3, 9.61) * mm});
            skLineSegment(sketch, "E419", {"start": v(-67.3, 9.61) * mm, "end": v(-67.28, 9.7) * mm});
            skLineSegment(sketch, "E420", {"start": v(-67.28, 9.7) * mm, "end": v(-66.62, 9.82) * mm});
            skLineSegment(sketch, "E421", {"start": v(-66.62, 9.82) * mm, "end": v(-66.56, 9.74) * mm});
            skLineSegment(sketch, "E422", {"start": v(-66.56, 9.74) * mm, "end": v(-66.5, 9.65) * mm});
            skLineSegment(sketch, "E423", {"start": v(-66.5, 9.65) * mm, "end": v(-66.43, 9.54) * mm});
            skLineSegment(sketch, "E424", {"start": v(-66.43, 9.54) * mm, "end": v(-66.37, 9.44) * mm});
            skLineSegment(sketch, "E425", {"start": v(-66.37, 9.44) * mm, "end": v(-66.32, 9.34) * mm});
            skLineSegment(sketch, "E426", {"start": v(-66.32, 9.34) * mm, "end": v(-66.27, 9.24) * mm});
            skLineSegment(sketch, "E427", {"start": v(-66.27, 9.24) * mm, "end": v(-66.23, 9.14) * mm});
            skLineSegment(sketch, "E428", {"start": v(-66.23, 9.14) * mm, "end": v(-66.2, 9.03) * mm});
            skLineSegment(sketch, "E429", {"start": v(-66.2, 9.03) * mm, "end": v(-66.2, 8.98) * mm});
            skLineSegment(sketch, "E430", {"start": v(-66.2, 8.98) * mm, "end": v(-66.16, 8.93) * mm});
            skLineSegment(sketch, "E431", {"start": v(-66.16, 8.93) * mm, "end": v(-66.13, 8.88) * mm});
            skLineSegment(sketch, "E432", {"start": v(-66.13, 8.88) * mm, "end": v(-66.11, 8.85) * mm});
            skLineSegment(sketch, "E433", {"start": v(-66.11, 8.85) * mm, "end": v(-66.08, 8.83) * mm});
            skLineSegment(sketch, "E434", {"start": v(-66.08, 8.83) * mm, "end": v(-66, 8.8) * mm});
            skLineSegment(sketch, "E435", {"start": v(-66, 8.8) * mm, "end": v(-65.5, 8.8) * mm});
            skLineSegment(sketch, "E436", {"start": v(-65.5, 8.8) * mm, "end": v(-65.43, 8.83) * mm});
            skLineSegment(sketch, "E437", {"start": v(-65.43, 8.83) * mm, "end": v(-65.4, 8.85) * mm});
            skLineSegment(sketch, "E438", {"start": v(-65.4, 8.85) * mm, "end": v(-65.37, 8.88) * mm});
            skLineSegment(sketch, "E439", {"start": v(-65.37, 8.88) * mm, "end": v(-65.34, 8.93) * mm});
            skLineSegment(sketch, "E440", {"start": v(-65.34, 8.93) * mm, "end": v(-65.32, 8.98) * mm});
            skLineSegment(sketch, "E441", {"start": v(-65.32, 8.98) * mm, "end": v(-65.3, 9.03) * mm});
            skLineSegment(sketch, "E442", {"start": v(-65.3, 9.03) * mm, "end": v(-65.27, 9.14) * mm});
            skLineSegment(sketch, "E443", {"start": v(-65.27, 9.14) * mm, "end": v(-65.24, 9.24) * mm});
            skLineSegment(sketch, "E444", {"start": v(-65.24, 9.24) * mm, "end": v(-65.19, 9.34) * mm});
            skLineSegment(sketch, "E445", {"start": v(-65.19, 9.34) * mm, "end": v(-65.14, 9.44) * mm});
            skLineSegment(sketch, "E446", {"start": v(-65.14, 9.44) * mm, "end": v(-65.08, 9.54) * mm});
            skLineSegment(sketch, "E447", {"start": v(-65.08, 9.54) * mm, "end": v(-65.02, 9.65) * mm});
            skLineSegment(sketch, "E448", {"start": v(-65.02, 9.65) * mm, "end": v(-64.95, 9.74) * mm});
            skLineSegment(sketch, "E449", {"start": v(-64.95, 9.74) * mm, "end": v(-64.9, 9.82) * mm});
            skLineSegment(sketch, "E450", {"start": v(-64.9, 9.82) * mm, "end": v(-64.23, 9.7) * mm});
            skLineSegment(sketch, "E451", {"start": v(-64.23, 9.7) * mm, "end": v(-64.2, 9.61) * mm});
            skLineSegment(sketch, "E452", {"start": v(-64.2, 9.61) * mm, "end": v(-64.17, 9.5) * mm});
            skLineSegment(sketch, "E453", {"start": v(-64.17, 9.5) * mm, "end": v(-64.15, 9.38) * mm});
            skLineSegment(sketch, "E454", {"start": v(-64.15, 9.38) * mm, "end": v(-64.13, 9.27) * mm});
            skLineSegment(sketch, "E455", {"start": v(-64.13, 9.27) * mm, "end": v(-64.11, 9.15) * mm});
            skLineSegment(sketch, "E456", {"start": v(-64.11, 9.15) * mm, "end": v(-64.1, 9.04) * mm});
            skLineSegment(sketch, "E457", {"start": v(-64.1, 9.04) * mm, "end": v(-64.1, 8.93) * mm});
            skLineSegment(sketch, "E458", {"start": v(-64.1, 8.93) * mm, "end": v(-64.1, 8.82) * mm});
            skLineSegment(sketch, "E459", {"start": v(-64.1, 8.82) * mm, "end": v(-64.12, 8.77) * mm});
            skLineSegment(sketch, "E460", {"start": v(-64.12, 8.77) * mm, "end": v(-64.1, 8.7) * mm});
            skLineSegment(sketch, "E461", {"start": v(-64.1, 8.7) * mm, "end": v(-64.1, 8.65) * mm});
            skLineSegment(sketch, "E462", {"start": v(-64.1, 8.65) * mm, "end": v(-64.09, 8.62) * mm});
            skLineSegment(sketch, "E463", {"start": v(-64.09, 8.62) * mm, "end": v(-64.07, 8.59) * mm});
            skLineSegment(sketch, "E464", {"start": v(-64.07, 8.59) * mm, "end": v(-64, 8.54) * mm});
            skLineSegment(sketch, "E465", {"start": v(-64, 8.54) * mm, "end": v(-63.53, 8.37) * mm});
            skLineSegment(sketch, "E466", {"start": v(-63.53, 8.37) * mm, "end": v(-63.45, 8.36) * mm});
            skLineSegment(sketch, "E467", {"start": v(-63.45, 8.36) * mm, "end": v(-63.41, 8.38) * mm});
            skLineSegment(sketch, "E468", {"start": v(-63.41, 8.38) * mm, "end": v(-63.38, 8.4) * mm});
            skLineSegment(sketch, "E469", {"start": v(-63.38, 8.4) * mm, "end": v(-63.34, 8.43) * mm});
            skLineSegment(sketch, "E470", {"start": v(-63.34, 8.43) * mm, "end": v(-63.3, 8.47) * mm});
            skLineSegment(sketch, "E471", {"start": v(-63.3, 8.47) * mm, "end": v(-63.27, 8.51) * mm});
            skLineSegment(sketch, "E472", {"start": v(-63.27, 8.51) * mm, "end": v(-63.2, 8.6) * mm});
            skLineSegment(sketch, "E473", {"start": v(-63.2, 8.6) * mm, "end": v(-63.13, 8.68) * mm});
            skLineSegment(sketch, "E474", {"start": v(-63.13, 8.68) * mm, "end": v(-63.05, 8.77) * mm});
            skLineSegment(sketch, "E475", {"start": v(-63.05, 8.77) * mm, "end": v(-62.97, 8.84) * mm});
            skLineSegment(sketch, "E476", {"start": v(-62.97, 8.84) * mm, "end": v(-62.88, 8.92) * mm});
            skLineSegment(sketch, "E477", {"start": v(-62.88, 8.92) * mm, "end": v(-62.78, 9) * mm});
            skLineSegment(sketch, "E478", {"start": v(-62.78, 9) * mm, "end": v(-62.69, 9.06) * mm});
            skLineSegment(sketch, "E479", {"start": v(-62.69, 9.06) * mm, "end": v(-62.61, 9.11) * mm});
            skLineSegment(sketch, "E480", {"start": v(-62.61, 9.11) * mm, "end": v(-62.02, 8.77) * mm});
            skLineSegment(sketch, "E481", {"start": v(-62.02, 8.77) * mm, "end": v(-62.03, 8.68) * mm});
            skLineSegment(sketch, "E482", {"start": v(-62.03, 8.68) * mm, "end": v(-62.04, 8.56) * mm});
            skLineSegment(sketch, "E483", {"start": v(-62.04, 8.56) * mm, "end": v(-62.06, 8.45) * mm});
            skLineSegment(sketch, "E484", {"start": v(-62.06, 8.45) * mm, "end": v(-62.08, 8.33) * mm});
            skLineSegment(sketch, "E485", {"start": v(-62.08, 8.33) * mm, "end": v(-62.1, 8.22) * mm});
            skLineSegment(sketch, "E486", {"start": v(-62.1, 8.22) * mm, "end": v(-62.14, 8.11) * mm});
            skLineSegment(sketch, "E487", {"start": v(-62.14, 8.11) * mm, "end": v(-62.17, 8) * mm});
            skLineSegment(sketch, "E488", {"start": v(-62.17, 8) * mm, "end": v(-62.21, 7.9) * mm});
            skLineSegment(sketch, "E489", {"start": v(-62.21, 7.9) * mm, "end": v(-62.24, 7.86) * mm});
            skLineSegment(sketch, "E490", {"start": v(-62.24, 7.86) * mm, "end": v(-62.25, 7.8) * mm});
            skLineSegment(sketch, "E491", {"start": v(-62.25, 7.8) * mm, "end": v(-62.26, 7.74) * mm});
            skLineSegment(sketch, "E492", {"start": v(-62.26, 7.74) * mm, "end": v(-62.26, 7.7) * mm});
            skLineSegment(sketch, "E493", {"start": v(-62.26, 7.7) * mm, "end": v(-62.26, 7.67) * mm});
            skLineSegment(sketch, "E494", {"start": v(-62.26, 7.67) * mm, "end": v(-62.21, 7.6) * mm});
            skLineSegment(sketch, "E495", {"start": v(-62.21, 7.6) * mm, "end": v(-61.82, 7.28) * mm});
            skLineSegment(sketch, "E496", {"start": v(-61.82, 7.28) * mm, "end": v(-61.75, 7.25) * mm});
            skLineSegment(sketch, "E497", {"start": v(-61.75, 7.25) * mm, "end": v(-61.71, 7.25) * mm});
            skLineSegment(sketch, "E498", {"start": v(-61.71, 7.25) * mm, "end": v(-61.68, 7.26) * mm});
            skLineSegment(sketch, "E499", {"start": v(-61.68, 7.26) * mm, "end": v(-61.62, 7.27) * mm});
            skLineSegment(sketch, "E500", {"start": v(-61.62, 7.27) * mm, "end": v(-61.57, 7.3) * mm});
            skLineSegment(sketch, "E501", {"start": v(-61.57, 7.3) * mm, "end": v(-61.53, 7.33) * mm});
            skLineSegment(sketch, "E502", {"start": v(-61.53, 7.33) * mm, "end": v(-61.44, 7.39) * mm});
            skLineSegment(sketch, "E503", {"start": v(-61.44, 7.39) * mm, "end": v(-61.34, 7.44) * mm});
            skLineSegment(sketch, "E504", {"start": v(-61.34, 7.44) * mm, "end": v(-61.24, 7.5) * mm});
            skLineSegment(sketch, "E505", {"start": v(-61.24, 7.5) * mm, "end": v(-61.13, 7.54) * mm});
            skLineSegment(sketch, "E506", {"start": v(-61.13, 7.54) * mm, "end": v(-61.02, 7.58) * mm});
            skLineSegment(sketch, "E507", {"start": v(-61.02, 7.58) * mm, "end": v(-60.91, 7.61) * mm});
            skLineSegment(sketch, "E508", {"start": v(-60.91, 7.61) * mm, "end": v(-60.8, 7.65) * mm});
            skLineSegment(sketch, "E509", {"start": v(-60.8, 7.65) * mm, "end": v(-60.7, 7.67) * mm});
            skLineSegment(sketch, "E510", {"start": v(-60.7, 7.67) * mm, "end": v(-60.27, 7.15) * mm});
            skLineSegment(sketch, "E511", {"start": v(-60.27, 7.15) * mm, "end": v(-60.3, 7.07) * mm});
            skLineSegment(sketch, "E512", {"start": v(-60.3, 7.07) * mm, "end": v(-60.36, 6.96) * mm});
            skLineSegment(sketch, "E513", {"start": v(-60.36, 6.96) * mm, "end": v(-60.42, 6.85) * mm});
            skLineSegment(sketch, "E514", {"start": v(-60.42, 6.85) * mm, "end": v(-60.47, 6.75) * mm});
            skLineSegment(sketch, "E515", {"start": v(-60.47, 6.75) * mm, "end": v(-60.54, 6.66) * mm});
            skLineSegment(sketch, "E516", {"start": v(-60.54, 6.66) * mm, "end": v(-60.6, 6.56) * mm});
            skLineSegment(sketch, "E517", {"start": v(-60.6, 6.56) * mm, "end": v(-60.67, 6.48) * mm});
            skLineSegment(sketch, "E518", {"start": v(-60.67, 6.48) * mm, "end": v(-60.75, 6.4) * mm});
            skLineSegment(sketch, "E519", {"start": v(-60.75, 6.4) * mm, "end": v(-60.79, 6.36) * mm});
            skLineSegment(sketch, "E520", {"start": v(-60.79, 6.36) * mm, "end": v(-60.82, 6.31) * mm});
            skLineSegment(sketch, "E521", {"start": v(-60.82, 6.31) * mm, "end": v(-60.85, 6.26) * mm});
            skLineSegment(sketch, "E522", {"start": v(-60.85, 6.26) * mm, "end": v(-60.86, 6.23) * mm});
            skLineSegment(sketch, "E523", {"start": v(-60.86, 6.23) * mm, "end": v(-60.86, 6.2) * mm});
            skLineSegment(sketch, "E524", {"start": v(-60.86, 6.2) * mm, "end": v(-60.85, 6.12) * mm});
            skLineSegment(sketch, "E525", {"start": v(-60.85, 6.12) * mm, "end": v(-60.6, 5.68) * mm});
            skLineSegment(sketch, "E526", {"start": v(-60.6, 5.68) * mm, "end": v(-60.54, 5.62) * mm});
            skLineSegment(sketch, "E527", {"start": v(-60.54, 5.62) * mm, "end": v(-60.5, 5.61) * mm});
            skLineSegment(sketch, "E528", {"start": v(-60.5, 5.61) * mm, "end": v(-60.47, 5.6) * mm});
            skLineSegment(sketch, "E529", {"start": v(-60.47, 5.6) * mm, "end": v(-60.4, 5.6) * mm});
            skLineSegment(sketch, "E530", {"start": v(-60.4, 5.6) * mm, "end": v(-60.35, 5.6) * mm});
            skLineSegment(sketch, "E531", {"start": v(-60.35, 5.6) * mm, "end": v(-60.3, 5.62) * mm});
            skLineSegment(sketch, "E532", {"start": v(-60.3, 5.62) * mm, "end": v(-60.2, 5.65) * mm});
            skLineSegment(sketch, "E533", {"start": v(-60.2, 5.65) * mm, "end": v(-60.08, 5.66) * mm});
            skLineSegment(sketch, "E534", {"start": v(-60.08, 5.66) * mm, "end": v(-59.97, 5.68) * mm});
            skLineSegment(sketch, "E535", {"start": v(-59.97, 5.68) * mm, "end": v(-59.86, 5.68) * mm});
            skLineSegment(sketch, "E536", {"start": v(-59.86, 5.68) * mm, "end": v(-59.74, 5.68) * mm});
            skLineSegment(sketch, "E537", {"start": v(-59.74, 5.68) * mm, "end": v(-59.62, 5.68) * mm});
            skLineSegment(sketch, "E538", {"start": v(-59.62, 5.68) * mm, "end": v(-59.5, 5.67) * mm});
            skLineSegment(sketch, "E539", {"start": v(-59.5, 5.67) * mm, "end": v(-59.41, 5.66) * mm});
            skLineSegment(sketch, "E540", {"start": v(-59.41, 5.66) * mm, "end": v(-59.18, 5.02) * mm});
            skLineSegment(sketch, "E541", {"start": v(-59.18, 5.02) * mm, "end": v(-59.24, 4.96) * mm});
            skLineSegment(sketch, "E542", {"start": v(-59.24, 4.96) * mm, "end": v(-59.33, 4.87) * mm});
            skLineSegment(sketch, "E543", {"start": v(-59.33, 4.87) * mm, "end": v(-59.42, 4.8) * mm});
            skLineSegment(sketch, "E544", {"start": v(-59.42, 4.8) * mm, "end": v(-59.5, 4.72) * mm});
            skLineSegment(sketch, "E545", {"start": v(-59.5, 4.72) * mm, "end": v(-59.6, 4.65) * mm});
            skLineSegment(sketch, "E546", {"start": v(-59.6, 4.65) * mm, "end": v(-59.7, 4.59) * mm});
            skLineSegment(sketch, "E547", {"start": v(-59.7, 4.59) * mm, "end": v(-59.79, 4.53) * mm});
            skLineSegment(sketch, "E548", {"start": v(-59.79, 4.53) * mm, "end": v(-59.88, 4.48) * mm});
            skLineSegment(sketch, "E549", {"start": v(-59.88, 4.48) * mm, "end": v(-59.93, 4.46) * mm});
            skLineSegment(sketch, "E550", {"start": v(-59.93, 4.46) * mm, "end": v(-59.98, 4.43) * mm});
            skLineSegment(sketch, "E551", {"start": v(-59.98, 4.43) * mm, "end": v(-60.02, 4.39) * mm});
            skLineSegment(sketch, "E552", {"start": v(-60.02, 4.39) * mm, "end": v(-60.05, 4.36) * mm});
            skLineSegment(sketch, "E553", {"start": v(-60.05, 4.36) * mm, "end": v(-60.06, 4.33) * mm});
            skLineSegment(sketch, "E554", {"start": v(-60.06, 4.33) * mm, "end": v(-60.07, 4.25) * mm});
            skLineSegment(sketch, "E555", {"start": v(-60.07, 4.25) * mm, "end": v(-59.99, 3.75) * mm});
            skCircle(sketch, "E556", {"center": v(-65.75, 3) * mm, "radius": 1.59 * mm});
            skLineSegment(sketch, "E557", {"start": v(-58.86, 3.25) * mm, "end": v(-58.87, 3.31) * mm});
            skLineSegment(sketch, "E558", {"start": v(-58.87, 3.31) * mm, "end": v(-58.89, 3.34) * mm});
            skLineSegment(sketch, "E559", {"start": v(-58.89, 3.34) * mm, "end": v(-58.9, 3.35) * mm});
            skLineSegment(sketch, "E560", {"start": v(-58.9, 3.35) * mm, "end": v(-58.92, 3.37) * mm});
            skLineSegment(sketch, "E561", {"start": v(-58.92, 3.37) * mm, "end": v(-58.93, 3.38) * mm});
            skLineSegment(sketch, "E562", {"start": v(-58.93, 3.38) * mm, "end": v(-58.97, 3.4) * mm});
            skLineSegment(sketch, "E563", {"start": v(-58.97, 3.4) * mm, "end": v(-59, 3.42) * mm});
            skLineSegment(sketch, "E564", {"start": v(-59, 3.42) * mm, "end": v(-59.03, 3.43) * mm});
            skLineSegment(sketch, "E565", {"start": v(-59.03, 3.43) * mm, "end": v(-59.07, 3.44) * mm});
            skLineSegment(sketch, "E566", {"start": v(-59.07, 3.44) * mm, "end": v(-59.14, 3.46) * mm});
            skLineSegment(sketch, "E567", {"start": v(-59.14, 3.46) * mm, "end": v(-59.2, 3.47) * mm});
            skLineSegment(sketch, "E568", {"start": v(-59.2, 3.47) * mm, "end": v(-59.27, 3.5) * mm});
            skLineSegment(sketch, "E569", {"start": v(-59.27, 3.5) * mm, "end": v(-59.34, 3.53) * mm});
            skLineSegment(sketch, "E570", {"start": v(-59.34, 3.53) * mm, "end": v(-59.4, 3.57) * mm});
            skLineSegment(sketch, "E571", {"start": v(-59.4, 3.57) * mm, "end": v(-59.47, 3.62) * mm});
            skLineSegment(sketch, "E572", {"start": v(-59.47, 3.62) * mm, "end": v(-59.53, 3.66) * mm});
            skLineSegment(sketch, "E573", {"start": v(-59.53, 3.66) * mm, "end": v(-59.6, 3.72) * mm});
            skLineSegment(sketch, "E574", {"start": v(-59.6, 3.72) * mm, "end": v(-59.65, 3.77) * mm});
            skLineSegment(sketch, "E575", {"start": v(-59.65, 3.77) * mm, "end": v(-59.71, 3.83) * mm});
            skLineSegment(sketch, "E576", {"start": v(-59.71, 3.83) * mm, "end": v(-59.77, 3.9) * mm});
            skLineSegment(sketch, "E577", {"start": v(-59.77, 3.9) * mm, "end": v(-59.81, 3.95) * mm});
            skLineSegment(sketch, "E578", {"start": v(-59.81, 3.95) * mm, "end": v(-59.71, 4.26) * mm});
            skLineSegment(sketch, "E579", {"start": v(-59.71, 4.26) * mm, "end": v(-59.59, 4.56) * mm});
            skLineSegment(sketch, "E580", {"start": v(-59.59, 4.56) * mm, "end": v(-59.52, 4.57) * mm});
            skLineSegment(sketch, "E581", {"start": v(-59.52, 4.57) * mm, "end": v(-59.44, 4.58) * mm});
            skLineSegment(sketch, "E582", {"start": v(-59.44, 4.58) * mm, "end": v(-59.36, 4.6) * mm});
            skLineSegment(sketch, "E583", {"start": v(-59.36, 4.6) * mm, "end": v(-59.27, 4.6) * mm});
            skLineSegment(sketch, "E584", {"start": v(-59.27, 4.6) * mm, "end": v(-59.2, 4.6) * mm});
            skLineSegment(sketch, "E585", {"start": v(-59.2, 4.6) * mm, "end": v(-59.11, 4.6) * mm});
            skLineSegment(sketch, "E586", {"start": v(-59.11, 4.6) * mm, "end": v(-59.04, 4.59) * mm});
            skLineSegment(sketch, "E587", {"start": v(-59.04, 4.59) * mm, "end": v(-58.96, 4.57) * mm});
            skLineSegment(sketch, "E588", {"start": v(-58.96, 4.57) * mm, "end": v(-58.89, 4.56) * mm});
            skLineSegment(sketch, "E589", {"start": v(-58.89, 4.56) * mm, "end": v(-58.82, 4.53) * mm});
            skLineSegment(sketch, "E590", {"start": v(-58.82, 4.53) * mm, "end": v(-58.76, 4.5) * mm});
            skLineSegment(sketch, "E591", {"start": v(-58.76, 4.5) * mm, "end": v(-58.7, 4.47) * mm});
            skLineSegment(sketch, "E592", {"start": v(-58.7, 4.47) * mm, "end": v(-58.66, 4.45) * mm});
            skLineSegment(sketch, "E593", {"start": v(-58.66, 4.45) * mm, "end": v(-58.63, 4.44) * mm});
            skLineSegment(sketch, "E594", {"start": v(-58.63, 4.44) * mm, "end": v(-58.6, 4.43) * mm});
            skLineSegment(sketch, "E595", {"start": v(-58.6, 4.43) * mm, "end": v(-58.55, 4.43) * mm});
            skLineSegment(sketch, "E596", {"start": v(-58.55, 4.43) * mm, "end": v(-58.53, 4.43) * mm});
            skLineSegment(sketch, "E597", {"start": v(-58.53, 4.43) * mm, "end": v(-58.5, 4.43) * mm});
            skLineSegment(sketch, "E598", {"start": v(-58.5, 4.43) * mm, "end": v(-58.49, 4.43) * mm});
            skLineSegment(sketch, "E599", {"start": v(-58.49, 4.43) * mm, "end": v(-58.46, 4.44) * mm});
            skLineSegment(sketch, "E600", {"start": v(-58.46, 4.44) * mm, "end": v(-58.41, 4.48) * mm});
            skLineSegment(sketch, "E601", {"start": v(-58.41, 4.48) * mm, "end": v(-58.25, 4.69) * mm});
            skLineSegment(sketch, "E602", {"start": v(-58.25, 4.69) * mm, "end": v(-58.08, 4.88) * mm});
            skLineSegment(sketch, "E603", {"start": v(-58.08, 4.88) * mm, "end": v(-58.05, 4.93) * mm});
            skLineSegment(sketch, "E604", {"start": v(-58.05, 4.93) * mm, "end": v(-58.04, 4.96) * mm});
            skLineSegment(sketch, "E605", {"start": v(-58.04, 4.96) * mm, "end": v(-58.04, 4.99) * mm});
            skLineSegment(sketch, "E606", {"start": v(-58.04, 4.99) * mm, "end": v(-58.04, 5) * mm});
            skLineSegment(sketch, "E607", {"start": v(-58.04, 5) * mm, "end": v(-58.05, 5.03) * mm});
            skLineSegment(sketch, "E608", {"start": v(-58.05, 5.03) * mm, "end": v(-58.06, 5.07) * mm});
            skLineSegment(sketch, "E609", {"start": v(-58.06, 5.07) * mm, "end": v(-58.07, 5.1) * mm});
            skLineSegment(sketch, "E610", {"start": v(-58.07, 5.1) * mm, "end": v(-58.1, 5.13) * mm});
            skLineSegment(sketch, "E611", {"start": v(-58.1, 5.13) * mm, "end": v(-58.11, 5.16) * mm});
            skLineSegment(sketch, "E612", {"start": v(-58.11, 5.16) * mm, "end": v(-58.15, 5.22) * mm});
            skLineSegment(sketch, "E613", {"start": v(-58.15, 5.22) * mm, "end": v(-58.2, 5.27) * mm});
            skLineSegment(sketch, "E614", {"start": v(-58.2, 5.27) * mm, "end": v(-58.23, 5.34) * mm});
            skLineSegment(sketch, "E615", {"start": v(-58.23, 5.34) * mm, "end": v(-58.26, 5.4) * mm});
            skLineSegment(sketch, "E616", {"start": v(-58.26, 5.4) * mm, "end": v(-58.29, 5.48) * mm});
            skLineSegment(sketch, "E617", {"start": v(-58.29, 5.48) * mm, "end": v(-58.3, 5.55) * mm});
            skLineSegment(sketch, "E618", {"start": v(-58.3, 5.55) * mm, "end": v(-58.33, 5.63) * mm});
            skLineSegment(sketch, "E619", {"start": v(-58.33, 5.63) * mm, "end": v(-58.34, 5.7) * mm});
            skLineSegment(sketch, "E620", {"start": v(-58.34, 5.7) * mm, "end": v(-58.35, 5.8) * mm});
            skLineSegment(sketch, "E621", {"start": v(-58.35, 5.8) * mm, "end": v(-58.35, 5.87) * mm});
            skLineSegment(sketch, "E622", {"start": v(-58.35, 5.87) * mm, "end": v(-58.36, 5.96) * mm});
            skLineSegment(sketch, "E623", {"start": v(-58.36, 5.96) * mm, "end": v(-58.36, 6.03) * mm});
            skLineSegment(sketch, "E624", {"start": v(-58.36, 6.03) * mm, "end": v(-58.08, 6.2) * mm});
            skLineSegment(sketch, "E625", {"start": v(-58.08, 6.2) * mm, "end": v(-57.8, 6.35) * mm});
            skLineSegment(sketch, "E626", {"start": v(-57.8, 6.35) * mm, "end": v(-57.74, 6.32) * mm});
            skLineSegment(sketch, "E627", {"start": v(-57.74, 6.32) * mm, "end": v(-57.66, 6.27) * mm});
            skLineSegment(sketch, "E628", {"start": v(-57.66, 6.27) * mm, "end": v(-57.6, 6.23) * mm});
            skLineSegment(sketch, "E629", {"start": v(-57.6, 6.23) * mm, "end": v(-57.53, 6.18) * mm});
            skLineSegment(sketch, "E630", {"start": v(-57.53, 6.18) * mm, "end": v(-57.47, 6.13) * mm});
            skLineSegment(sketch, "E631", {"start": v(-57.47, 6.13) * mm, "end": v(-57.4, 6.07) * mm});
            skLineSegment(sketch, "E632", {"start": v(-57.4, 6.07) * mm, "end": v(-57.35, 6.02) * mm});
            skLineSegment(sketch, "E633", {"start": v(-57.35, 6.02) * mm, "end": v(-57.3, 5.96) * mm});
            skLineSegment(sketch, "E634", {"start": v(-57.3, 5.96) * mm, "end": v(-57.26, 5.9) * mm});
            skLineSegment(sketch, "E635", {"start": v(-57.26, 5.9) * mm, "end": v(-57.22, 5.84) * mm});
            skLineSegment(sketch, "E636", {"start": v(-57.22, 5.84) * mm, "end": v(-57.2, 5.77) * mm});
            skLineSegment(sketch, "E637", {"start": v(-57.2, 5.77) * mm, "end": v(-57.17, 5.7) * mm});
            skLineSegment(sketch, "E638", {"start": v(-57.17, 5.7) * mm, "end": v(-57.15, 5.67) * mm});
            skLineSegment(sketch, "E639", {"start": v(-57.15, 5.67) * mm, "end": v(-57.13, 5.64) * mm});
            skLineSegment(sketch, "E640", {"start": v(-57.13, 5.64) * mm, "end": v(-57.11, 5.61) * mm});
            skLineSegment(sketch, "E641", {"start": v(-57.11, 5.61) * mm, "end": v(-57.08, 5.58) * mm});
            skLineSegment(sketch, "E642", {"start": v(-57.08, 5.58) * mm, "end": v(-57.07, 5.57) * mm});
            skLineSegment(sketch, "E643", {"start": v(-57.07, 5.57) * mm, "end": v(-57.05, 5.56) * mm});
            skLineSegment(sketch, "E644", {"start": v(-57.05, 5.56) * mm, "end": v(-57.03, 5.55) * mm});
            skLineSegment(sketch, "E645", {"start": v(-57.03, 5.55) * mm, "end": v(-57, 5.54) * mm});
            skLineSegment(sketch, "E646", {"start": v(-57, 5.54) * mm, "end": v(-56.94, 5.54) * mm});
            skLineSegment(sketch, "E647", {"start": v(-56.94, 5.54) * mm, "end": v(-56.69, 5.6) * mm});
            skLineSegment(sketch, "E648", {"start": v(-56.69, 5.6) * mm, "end": v(-56.43, 5.63) * mm});
            skLineSegment(sketch, "E649", {"start": v(-56.43, 5.63) * mm, "end": v(-56.37, 5.65) * mm});
            skLineSegment(sketch, "E650", {"start": v(-56.37, 5.65) * mm, "end": v(-56.35, 5.67) * mm});
            skLineSegment(sketch, "E651", {"start": v(-56.35, 5.67) * mm, "end": v(-56.34, 5.68) * mm});
            skLineSegment(sketch, "E652", {"start": v(-56.34, 5.68) * mm, "end": v(-56.32, 5.7) * mm});
            skLineSegment(sketch, "E653", {"start": v(-56.32, 5.7) * mm, "end": v(-56.31, 5.72) * mm});
            skLineSegment(sketch, "E654", {"start": v(-56.31, 5.72) * mm, "end": v(-56.3, 5.76) * mm});
            skLineSegment(sketch, "E655", {"start": v(-56.3, 5.76) * mm, "end": v(-56.29, 5.8) * mm});
            skLineSegment(sketch, "E656", {"start": v(-56.29, 5.8) * mm, "end": v(-56.28, 5.83) * mm});
            skLineSegment(sketch, "E657", {"start": v(-56.28, 5.83) * mm, "end": v(-56.27, 5.86) * mm});
            skLineSegment(sketch, "E658", {"start": v(-56.27, 5.86) * mm, "end": v(-56.27, 5.93) * mm});
            skLineSegment(sketch, "E659", {"start": v(-56.27, 5.93) * mm, "end": v(-56.27, 6) * mm});
            skLineSegment(sketch, "E660", {"start": v(-56.27, 6) * mm, "end": v(-56.26, 6.08) * mm});
            skLineSegment(sketch, "E661", {"start": v(-56.26, 6.08) * mm, "end": v(-56.24, 6.15) * mm});
            skLineSegment(sketch, "E662", {"start": v(-56.24, 6.15) * mm, "end": v(-56.2, 6.22) * mm});
            skLineSegment(sketch, "E663", {"start": v(-56.2, 6.22) * mm, "end": v(-56.18, 6.29) * mm});
            skLineSegment(sketch, "E664", {"start": v(-56.18, 6.29) * mm, "end": v(-56.14, 6.36) * mm});
            skLineSegment(sketch, "E665", {"start": v(-56.14, 6.36) * mm, "end": v(-56.1, 6.43) * mm});
            skLineSegment(sketch, "E666", {"start": v(-56.1, 6.43) * mm, "end": v(-56.05, 6.5) * mm});
            skLineSegment(sketch, "E667", {"start": v(-56.05, 6.5) * mm, "end": v(-56, 6.57) * mm});
            skLineSegment(sketch, "E668", {"start": v(-56, 6.57) * mm, "end": v(-55.95, 6.63) * mm});
            skLineSegment(sketch, "E669", {"start": v(-55.95, 6.63) * mm, "end": v(-55.9, 6.68) * mm});
            skLineSegment(sketch, "E670", {"start": v(-55.9, 6.68) * mm, "end": v(-55.59, 6.64) * mm});
            skLineSegment(sketch, "E671", {"start": v(-55.59, 6.64) * mm, "end": v(-55.27, 6.57) * mm});
            skLineSegment(sketch, "E672", {"start": v(-55.27, 6.57) * mm, "end": v(-55.25, 6.5) * mm});
            skLineSegment(sketch, "E673", {"start": v(-55.25, 6.5) * mm, "end": v(-55.22, 6.43) * mm});
            skLineSegment(sketch, "E674", {"start": v(-55.22, 6.43) * mm, "end": v(-55.2, 6.35) * mm});
            skLineSegment(sketch, "E675", {"start": v(-55.2, 6.35) * mm, "end": v(-55.18, 6.27) * mm});
            skLineSegment(sketch, "E676", {"start": v(-55.18, 6.27) * mm, "end": v(-55.16, 6.19) * mm});
            skLineSegment(sketch, "E677", {"start": v(-55.16, 6.19) * mm, "end": v(-55.15, 6.1) * mm});
            skLineSegment(sketch, "E678", {"start": v(-55.15, 6.1) * mm, "end": v(-55.14, 6.03) * mm});
            skLineSegment(sketch, "E679", {"start": v(-55.14, 6.03) * mm, "end": v(-55.14, 5.96) * mm});
            skLineSegment(sketch, "E680", {"start": v(-55.14, 5.96) * mm, "end": v(-55.15, 5.88) * mm});
            skLineSegment(sketch, "E681", {"start": v(-55.15, 5.88) * mm, "end": v(-55.16, 5.8) * mm});
            skLineSegment(sketch, "E682", {"start": v(-55.16, 5.8) * mm, "end": v(-55.18, 5.74) * mm});
            skLineSegment(sketch, "E683", {"start": v(-55.18, 5.74) * mm, "end": v(-55.2, 5.67) * mm});
            skLineSegment(sketch, "E684", {"start": v(-55.2, 5.67) * mm, "end": v(-55.21, 5.64) * mm});
            skLineSegment(sketch, "E685", {"start": v(-55.21, 5.64) * mm, "end": v(-55.22, 5.6) * mm});
            skLineSegment(sketch, "E686", {"start": v(-55.22, 5.6) * mm, "end": v(-55.22, 5.57) * mm});
            skLineSegment(sketch, "E687", {"start": v(-55.22, 5.57) * mm, "end": v(-55.22, 5.53) * mm});
            skLineSegment(sketch, "E688", {"start": v(-55.22, 5.53) * mm, "end": v(-55.21, 5.5) * mm});
            skLineSegment(sketch, "E689", {"start": v(-55.21, 5.5) * mm, "end": v(-55.2, 5.49) * mm});
            skLineSegment(sketch, "E690", {"start": v(-55.2, 5.49) * mm, "end": v(-55.2, 5.46) * mm});
            skLineSegment(sketch, "E691", {"start": v(-55.2, 5.46) * mm, "end": v(-55.19, 5.44) * mm});
            skLineSegment(sketch, "E692", {"start": v(-55.19, 5.44) * mm, "end": v(-55.14, 5.4) * mm});
            skLineSegment(sketch, "E693", {"start": v(-55.14, 5.4) * mm, "end": v(-54.9, 5.28) * mm});
            skLineSegment(sketch, "E694", {"start": v(-54.9, 5.28) * mm, "end": v(-54.69, 5.14) * mm});
            skLineSegment(sketch, "E695", {"start": v(-54.69, 5.14) * mm, "end": v(-54.63, 5.12) * mm});
            skLineSegment(sketch, "E696", {"start": v(-54.63, 5.12) * mm, "end": v(-54.6, 5.12) * mm});
            skLineSegment(sketch, "E697", {"start": v(-54.6, 5.12) * mm, "end": v(-54.58, 5.12) * mm});
            skLineSegment(sketch, "E698", {"start": v(-54.58, 5.12) * mm, "end": v(-54.56, 5.13) * mm});
            skLineSegment(sketch, "E699", {"start": v(-54.56, 5.13) * mm, "end": v(-54.54, 5.14) * mm});
            skLineSegment(sketch, "E700", {"start": v(-54.54, 5.14) * mm, "end": v(-54.5, 5.15) * mm});
            skLineSegment(sketch, "E701", {"start": v(-54.5, 5.15) * mm, "end": v(-54.47, 5.17) * mm});
            skLineSegment(sketch, "E702", {"start": v(-54.47, 5.17) * mm, "end": v(-54.44, 5.2) * mm});
            skLineSegment(sketch, "E703", {"start": v(-54.44, 5.2) * mm, "end": v(-54.42, 5.22) * mm});
            skLineSegment(sketch, "E704", {"start": v(-54.42, 5.22) * mm, "end": v(-54.37, 5.27) * mm});
            skLineSegment(sketch, "E705", {"start": v(-54.37, 5.27) * mm, "end": v(-54.32, 5.33) * mm});
            skLineSegment(sketch, "E706", {"start": v(-54.32, 5.33) * mm, "end": v(-54.27, 5.37) * mm});
            skLineSegment(sketch, "E707", {"start": v(-54.27, 5.37) * mm, "end": v(-54.2, 5.41) * mm});
            skLineSegment(sketch, "E708", {"start": v(-54.2, 5.41) * mm, "end": v(-54.14, 5.45) * mm});
            skLineSegment(sketch, "E709", {"start": v(-54.14, 5.45) * mm, "end": v(-54.07, 5.48) * mm});
            skLineSegment(sketch, "E710", {"start": v(-54.07, 5.48) * mm, "end": v(-54, 5.51) * mm});
            skLineSegment(sketch, "E711", {"start": v(-54, 5.51) * mm, "end": v(-53.92, 5.54) * mm});
            skLineSegment(sketch, "E712", {"start": v(-53.92, 5.54) * mm, "end": v(-53.84, 5.56) * mm});
            skLineSegment(sketch, "E713", {"start": v(-53.84, 5.56) * mm, "end": v(-53.76, 5.58) * mm});
            skLineSegment(sketch, "E714", {"start": v(-53.76, 5.58) * mm, "end": v(-53.67, 5.6) * mm});
            skLineSegment(sketch, "E715", {"start": v(-53.67, 5.6) * mm, "end": v(-53.6, 5.61) * mm});
            skLineSegment(sketch, "E716", {"start": v(-53.6, 5.61) * mm, "end": v(-53.39, 5.37) * mm});
            skLineSegment(sketch, "E717", {"start": v(-53.39, 5.37) * mm, "end": v(-53.2, 5.12) * mm});
            skLineSegment(sketch, "E718", {"start": v(-53.2, 5.12) * mm, "end": v(-53.21, 5.05) * mm});
            skLineSegment(sketch, "E719", {"start": v(-53.21, 5.05) * mm, "end": v(-53.25, 4.97) * mm});
            skLineSegment(sketch, "E720", {"start": v(-53.25, 4.97) * mm, "end": v(-53.28, 4.9) * mm});
            skLineSegment(sketch, "E721", {"start": v(-53.28, 4.9) * mm, "end": v(-53.32, 4.82) * mm});
            skLineSegment(sketch, "E722", {"start": v(-53.32, 4.82) * mm, "end": v(-53.36, 4.75) * mm});
            skLineSegment(sketch, "E723", {"start": v(-53.36, 4.75) * mm, "end": v(-53.4, 4.69) * mm});
            skLineSegment(sketch, "E724", {"start": v(-53.4, 4.69) * mm, "end": v(-53.44, 4.62) * mm});
            skLineSegment(sketch, "E725", {"start": v(-53.44, 4.62) * mm, "end": v(-53.5, 4.56) * mm});
            skLineSegment(sketch, "E726", {"start": v(-53.5, 4.56) * mm, "end": v(-53.54, 4.5) * mm});
            skLineSegment(sketch, "E727", {"start": v(-53.54, 4.5) * mm, "end": v(-53.6, 4.46) * mm});
            skLineSegment(sketch, "E728", {"start": v(-53.6, 4.46) * mm, "end": v(-53.66, 4.43) * mm});
            skLineSegment(sketch, "E729", {"start": v(-53.66, 4.43) * mm, "end": v(-53.72, 4.39) * mm});
            skLineSegment(sketch, "E730", {"start": v(-53.72, 4.39) * mm, "end": v(-53.75, 4.37) * mm});
            skLineSegment(sketch, "E731", {"start": v(-53.75, 4.37) * mm, "end": v(-53.77, 4.34) * mm});
            skLineSegment(sketch, "E732", {"start": v(-53.77, 4.34) * mm, "end": v(-53.8, 4.31) * mm});
            skLineSegment(sketch, "E733", {"start": v(-53.8, 4.31) * mm, "end": v(-53.82, 4.28) * mm});
            skLineSegment(sketch, "E734", {"start": v(-53.82, 4.28) * mm, "end": v(-53.83, 4.27) * mm});
            skLineSegment(sketch, "E735", {"start": v(-53.83, 4.27) * mm, "end": v(-53.84, 4.25) * mm});
            skLineSegment(sketch, "E736", {"start": v(-53.84, 4.25) * mm, "end": v(-53.85, 4.22) * mm});
            skLineSegment(sketch, "E737", {"start": v(-53.85, 4.22) * mm, "end": v(-53.86, 4.2) * mm});
            skLineSegment(sketch, "E738", {"start": v(-53.86, 4.2) * mm, "end": v(-53.85, 4.13) * mm});
            skLineSegment(sketch, "E739", {"start": v(-53.85, 4.13) * mm, "end": v(-53.75, 3.9) * mm});
            skLineSegment(sketch, "E740", {"start": v(-53.75, 3.9) * mm, "end": v(-53.67, 3.65) * mm});
            skLineSegment(sketch, "E741", {"start": v(-53.67, 3.65) * mm, "end": v(-53.64, 3.6) * mm});
            skLineSegment(sketch, "E742", {"start": v(-53.64, 3.6) * mm, "end": v(-53.62, 3.57) * mm});
            skLineSegment(sketch, "E743", {"start": v(-53.62, 3.57) * mm, "end": v(-53.6, 3.56) * mm});
            skLineSegment(sketch, "E744", {"start": v(-53.6, 3.56) * mm, "end": v(-53.57, 3.55) * mm});
            skLineSegment(sketch, "E745", {"start": v(-53.57, 3.55) * mm, "end": v(-53.55, 3.55) * mm});
            skLineSegment(sketch, "E746", {"start": v(-53.55, 3.55) * mm, "end": v(-53.52, 3.54) * mm});
            skLineSegment(sketch, "E747", {"start": v(-53.52, 3.54) * mm, "end": v(-53.48, 3.53) * mm});
            skLineSegment(sketch, "E748", {"start": v(-53.48, 3.53) * mm, "end": v(-53.44, 3.53) * mm});
            skLineSegment(sketch, "E749", {"start": v(-53.44, 3.53) * mm, "end": v(-53.4, 3.53) * mm});
            skLineSegment(sketch, "E750", {"start": v(-53.4, 3.53) * mm, "end": v(-53.34, 3.54) * mm});
            skLineSegment(sketch, "E751", {"start": v(-53.34, 3.54) * mm, "end": v(-53.27, 3.56) * mm});
            skLineSegment(sketch, "E752", {"start": v(-53.27, 3.56) * mm, "end": v(-53.2, 3.55) * mm});
            skLineSegment(sketch, "E753", {"start": v(-53.2, 3.55) * mm, "end": v(-53.12, 3.54) * mm});
            skLineSegment(sketch, "E754", {"start": v(-53.12, 3.54) * mm, "end": v(-53.05, 3.53) * mm});
            skLineSegment(sketch, "E755", {"start": v(-53.05, 3.53) * mm, "end": v(-52.97, 3.51) * mm});
            skLineSegment(sketch, "E756", {"start": v(-52.97, 3.51) * mm, "end": v(-52.9, 3.49) * mm});
            skLineSegment(sketch, "E757", {"start": v(-52.9, 3.49) * mm, "end": v(-52.82, 3.46) * mm});
            skLineSegment(sketch, "E758", {"start": v(-52.82, 3.46) * mm, "end": v(-52.74, 3.43) * mm});
            skLineSegment(sketch, "E759", {"start": v(-52.74, 3.43) * mm, "end": v(-52.67, 3.39) * mm});
            skLineSegment(sketch, "E760", {"start": v(-52.67, 3.39) * mm, "end": v(-52.6, 3.35) * mm});
            skLineSegment(sketch, "E761", {"start": v(-52.6, 3.35) * mm, "end": v(-52.54, 3.31) * mm});
            skLineSegment(sketch, "E762", {"start": v(-52.54, 3.31) * mm, "end": v(-52.52, 3) * mm});
            skLineSegment(sketch, "E763", {"start": v(-52.52, 3) * mm, "end": v(-52.54, 2.67) * mm});
            skLineSegment(sketch, "E764", {"start": v(-52.54, 2.67) * mm, "end": v(-52.6, 2.63) * mm});
            skLineSegment(sketch, "E765", {"start": v(-52.6, 2.63) * mm, "end": v(-52.67, 2.6) * mm});
            skLineSegment(sketch, "E766", {"start": v(-52.67, 2.6) * mm, "end": v(-52.74, 2.56) * mm});
            skLineSegment(sketch, "E767", {"start": v(-52.74, 2.56) * mm, "end": v(-52.82, 2.52) * mm});
            skLineSegment(sketch, "E768", {"start": v(-52.82, 2.52) * mm, "end": v(-52.9, 2.5) * mm});
            skLineSegment(sketch, "E769", {"start": v(-52.9, 2.5) * mm, "end": v(-52.97, 2.47) * mm});
            skLineSegment(sketch, "E770", {"start": v(-52.97, 2.47) * mm, "end": v(-53.05, 2.45) * mm});
            skLineSegment(sketch, "E771", {"start": v(-53.05, 2.45) * mm, "end": v(-53.12, 2.44) * mm});
            skLineSegment(sketch, "E772", {"start": v(-53.12, 2.44) * mm, "end": v(-53.2, 2.43) * mm});
            skLineSegment(sketch, "E773", {"start": v(-53.2, 2.43) * mm, "end": v(-53.27, 2.43) * mm});
            skLineSegment(sketch, "E774", {"start": v(-53.27, 2.43) * mm, "end": v(-53.34, 2.44) * mm});
            skLineSegment(sketch, "E775", {"start": v(-53.34, 2.44) * mm, "end": v(-53.4, 2.45) * mm});
            skLineSegment(sketch, "E776", {"start": v(-53.4, 2.45) * mm, "end": v(-53.44, 2.45) * mm});
            skLineSegment(sketch, "E777", {"start": v(-53.44, 2.45) * mm, "end": v(-53.48, 2.45) * mm});
            skLineSegment(sketch, "E778", {"start": v(-53.48, 2.45) * mm, "end": v(-53.52, 2.44) * mm});
            skLineSegment(sketch, "E779", {"start": v(-53.52, 2.44) * mm, "end": v(-53.55, 2.43) * mm});
            skLineSegment(sketch, "E780", {"start": v(-53.55, 2.43) * mm, "end": v(-53.57, 2.43) * mm});
            skLineSegment(sketch, "E781", {"start": v(-53.57, 2.43) * mm, "end": v(-53.6, 2.42) * mm});
            skLineSegment(sketch, "E782", {"start": v(-53.6, 2.42) * mm, "end": v(-53.62, 2.4) * mm});
            skLineSegment(sketch, "E783", {"start": v(-53.62, 2.4) * mm, "end": v(-53.64, 2.39) * mm});
            skLineSegment(sketch, "E784", {"start": v(-53.64, 2.39) * mm, "end": v(-53.67, 2.33) * mm});
            skLineSegment(sketch, "E785", {"start": v(-53.67, 2.33) * mm, "end": v(-53.75, 2.09) * mm});
            skLineSegment(sketch, "E786", {"start": v(-53.75, 2.09) * mm, "end": v(-53.85, 1.85) * mm});
            skLineSegment(sketch, "E787", {"start": v(-53.85, 1.85) * mm, "end": v(-53.86, 1.79) * mm});
            skLineSegment(sketch, "E788", {"start": v(-53.86, 1.79) * mm, "end": v(-53.85, 1.76) * mm});
            skLineSegment(sketch, "E789", {"start": v(-53.85, 1.76) * mm, "end": v(-53.84, 1.73) * mm});
            skLineSegment(sketch, "E790", {"start": v(-53.84, 1.73) * mm, "end": v(-53.83, 1.72) * mm});
            skLineSegment(sketch, "E791", {"start": v(-53.83, 1.72) * mm, "end": v(-53.82, 1.7) * mm});
            skLineSegment(sketch, "E792", {"start": v(-53.82, 1.7) * mm, "end": v(-53.8, 1.67) * mm});
            skLineSegment(sketch, "E793", {"start": v(-53.8, 1.67) * mm, "end": v(-53.77, 1.64) * mm});
            skLineSegment(sketch, "E794", {"start": v(-53.77, 1.64) * mm, "end": v(-53.75, 1.62) * mm});
            skLineSegment(sketch, "E795", {"start": v(-53.75, 1.62) * mm, "end": v(-53.72, 1.6) * mm});
            skLineSegment(sketch, "E796", {"start": v(-53.72, 1.6) * mm, "end": v(-53.66, 1.56) * mm});
            skLineSegment(sketch, "E797", {"start": v(-53.66, 1.56) * mm, "end": v(-53.6, 1.52) * mm});
            skLineSegment(sketch, "E798", {"start": v(-53.6, 1.52) * mm, "end": v(-53.54, 1.47) * mm});
            skLineSegment(sketch, "E799", {"start": v(-53.54, 1.47) * mm, "end": v(-53.5, 1.42) * mm});
            skLineSegment(sketch, "E800", {"start": v(-53.5, 1.42) * mm, "end": v(-53.44, 1.36) * mm});
            skLineSegment(sketch, "E801", {"start": v(-53.44, 1.36) * mm, "end": v(-53.4, 1.3) * mm});
            skLineSegment(sketch, "E802", {"start": v(-53.4, 1.3) * mm, "end": v(-53.36, 1.23) * mm});
            skLineSegment(sketch, "E803", {"start": v(-53.36, 1.23) * mm, "end": v(-53.32, 1.16) * mm});
            skLineSegment(sketch, "E804", {"start": v(-53.32, 1.16) * mm, "end": v(-53.28, 1.08) * mm});
            skLineSegment(sketch, "E805", {"start": v(-53.28, 1.08) * mm, "end": v(-53.25, 1) * mm});
            skLineSegment(sketch, "E806", {"start": v(-53.25, 1) * mm, "end": v(-53.21, 0.93) * mm});
            skLineSegment(sketch, "E807", {"start": v(-53.21, 0.93) * mm, "end": v(-53.2, 0.86) * mm});
            skLineSegment(sketch, "E808", {"start": v(-53.2, 0.86) * mm, "end": v(-53.39, 0.6) * mm});
            skLineSegment(sketch, "E809", {"start": v(-53.39, 0.6) * mm, "end": v(-53.6, 0.37) * mm});
            skLineSegment(sketch, "E810", {"start": v(-53.6, 0.37) * mm, "end": v(-53.67, 0.38) * mm});
            skLineSegment(sketch, "E811", {"start": v(-53.67, 0.38) * mm, "end": v(-53.76, 0.4) * mm});
            skLineSegment(sketch, "E812", {"start": v(-53.76, 0.4) * mm, "end": v(-53.84, 0.42) * mm});
            skLineSegment(sketch, "E813", {"start": v(-53.84, 0.42) * mm, "end": v(-53.92, 0.44) * mm});
            skLineSegment(sketch, "E814", {"start": v(-53.92, 0.44) * mm, "end": v(-54, 0.47) * mm});
            skLineSegment(sketch, "E815", {"start": v(-54, 0.47) * mm, "end": v(-54.07, 0.5) * mm});
            skLineSegment(sketch, "E816", {"start": v(-54.07, 0.5) * mm, "end": v(-54.14, 0.53) * mm});
            skLineSegment(sketch, "E817", {"start": v(-54.14, 0.53) * mm, "end": v(-54.2, 0.57) * mm});
            skLineSegment(sketch, "E818", {"start": v(-54.2, 0.57) * mm, "end": v(-54.27, 0.6) * mm});
            skLineSegment(sketch, "E819", {"start": v(-54.27, 0.6) * mm, "end": v(-54.32, 0.65) * mm});
            skLineSegment(sketch, "E820", {"start": v(-54.32, 0.65) * mm, "end": v(-54.37, 0.7) * mm});
            skLineSegment(sketch, "E821", {"start": v(-54.37, 0.7) * mm, "end": v(-54.42, 0.76) * mm});
            skLineSegment(sketch, "E822", {"start": v(-54.42, 0.76) * mm, "end": v(-54.44, 0.78) * mm});
            skLineSegment(sketch, "E823", {"start": v(-54.44, 0.78) * mm, "end": v(-54.47, 0.8) * mm});
            skLineSegment(sketch, "E824", {"start": v(-54.47, 0.8) * mm, "end": v(-54.5, 0.83) * mm});
            skLineSegment(sketch, "E825", {"start": v(-54.5, 0.83) * mm, "end": v(-54.54, 0.84) * mm});
            skLineSegment(sketch, "E826", {"start": v(-54.54, 0.84) * mm, "end": v(-54.56, 0.85) * mm});
            skLineSegment(sketch, "E827", {"start": v(-54.56, 0.85) * mm, "end": v(-54.58, 0.86) * mm});
            skLineSegment(sketch, "E828", {"start": v(-54.58, 0.86) * mm, "end": v(-54.6, 0.86) * mm});
            skLineSegment(sketch, "E829", {"start": v(-54.6, 0.86) * mm, "end": v(-54.63, 0.86) * mm});
            skLineSegment(sketch, "E830", {"start": v(-54.63, 0.86) * mm, "end": v(-54.69, 0.84) * mm});
            skLineSegment(sketch, "E831", {"start": v(-54.69, 0.84) * mm, "end": v(-54.9, 0.7) * mm});
            skLineSegment(sketch, "E832", {"start": v(-54.9, 0.7) * mm, "end": v(-55.14, 0.58) * mm});
            skLineSegment(sketch, "E833", {"start": v(-55.14, 0.58) * mm, "end": v(-55.19, 0.54) * mm});
            skLineSegment(sketch, "E834", {"start": v(-55.19, 0.54) * mm, "end": v(-55.2, 0.52) * mm});
            skLineSegment(sketch, "E835", {"start": v(-55.2, 0.52) * mm, "end": v(-55.2, 0.5) * mm});
            skLineSegment(sketch, "E836", {"start": v(-55.2, 0.5) * mm, "end": v(-55.21, 0.47) * mm});
            skLineSegment(sketch, "E837", {"start": v(-55.21, 0.47) * mm, "end": v(-55.22, 0.45) * mm});
            skLineSegment(sketch, "E838", {"start": v(-55.22, 0.45) * mm, "end": v(-55.22, 0.41) * mm});
            skLineSegment(sketch, "E839", {"start": v(-55.22, 0.41) * mm, "end": v(-55.22, 0.38) * mm});
            skLineSegment(sketch, "E840", {"start": v(-55.22, 0.38) * mm, "end": v(-55.21, 0.34) * mm});
            skLineSegment(sketch, "E841", {"start": v(-55.21, 0.34) * mm, "end": v(-55.2, 0.3) * mm});
            skLineSegment(sketch, "E842", {"start": v(-55.2, 0.3) * mm, "end": v(-55.18, 0.24) * mm});
            skLineSegment(sketch, "E843", {"start": v(-55.18, 0.24) * mm, "end": v(-55.16, 0.17) * mm});
            skLineSegment(sketch, "E844", {"start": v(-55.16, 0.17) * mm, "end": v(-55.15, 0.1) * mm});
            skLineSegment(sketch, "E845", {"start": v(-55.15, 0.1) * mm, "end": v(-55.14, 0.03) * mm});
            skLineSegment(sketch, "E846", {"start": v(-55.14, 0.03) * mm, "end": v(-55.14, -0.05) * mm});
            skLineSegment(sketch, "E847", {"start": v(-55.14, -0.05) * mm, "end": v(-55.15, -0.13) * mm});
            skLineSegment(sketch, "E848", {"start": v(-55.15, -0.13) * mm, "end": v(-55.16, -0.2) * mm});
            skLineSegment(sketch, "E849", {"start": v(-55.16, -0.2) * mm, "end": v(-55.18, -0.29) * mm});
            skLineSegment(sketch, "E850", {"start": v(-55.18, -0.29) * mm, "end": v(-55.2, -0.37) * mm});
            skLineSegment(sketch, "E851", {"start": v(-55.2, -0.37) * mm, "end": v(-55.22, -0.45) * mm});
            skLineSegment(sketch, "E852", {"start": v(-55.22, -0.45) * mm, "end": v(-55.25, -0.53) * mm});
            skLineSegment(sketch, "E853", {"start": v(-55.25, -0.53) * mm, "end": v(-55.27, -0.59) * mm});
            skLineSegment(sketch, "E854", {"start": v(-55.27, -0.59) * mm, "end": v(-55.59, -0.66) * mm});
            skLineSegment(sketch, "E855", {"start": v(-55.59, -0.66) * mm, "end": v(-55.9, -0.7) * mm});
            skLineSegment(sketch, "E856", {"start": v(-55.9, -0.7) * mm, "end": v(-55.95, -0.65) * mm});
            skLineSegment(sketch, "E857", {"start": v(-55.95, -0.65) * mm, "end": v(-56, -0.59) * mm});
            skLineSegment(sketch, "E858", {"start": v(-56, -0.59) * mm, "end": v(-56.05, -0.52) * mm});
            skLineSegment(sketch, "E859", {"start": v(-56.05, -0.52) * mm, "end": v(-56.1, -0.45) * mm});
            skLineSegment(sketch, "E860", {"start": v(-56.1, -0.45) * mm, "end": v(-56.14, -0.38) * mm});
            skLineSegment(sketch, "E861", {"start": v(-56.14, -0.38) * mm, "end": v(-56.18, -0.3) * mm});
            skLineSegment(sketch, "E862", {"start": v(-56.18, -0.3) * mm, "end": v(-56.2, -0.24) * mm});
            skLineSegment(sketch, "E863", {"start": v(-56.2, -0.24) * mm, "end": v(-56.24, -0.17) * mm});
            skLineSegment(sketch, "E864", {"start": v(-56.24, -0.17) * mm, "end": v(-56.26, -0.1) * mm});
            skLineSegment(sketch, "E865", {"start": v(-56.26, -0.1) * mm, "end": v(-56.27, -0.02) * mm});
            skLineSegment(sketch, "E866", {"start": v(-56.27, -0.02) * mm, "end": v(-56.27, 0.05) * mm});
            skLineSegment(sketch, "E867", {"start": v(-56.27, 0.05) * mm, "end": v(-56.27, 0.12) * mm});
            skLineSegment(sketch, "E868", {"start": v(-56.27, 0.12) * mm, "end": v(-56.28, 0.15) * mm});
            skLineSegment(sketch, "E869", {"start": v(-56.28, 0.15) * mm, "end": v(-56.29, 0.19) * mm});
            skLineSegment(sketch, "E870", {"start": v(-56.29, 0.19) * mm, "end": v(-56.3, 0.22) * mm});
            skLineSegment(sketch, "E871", {"start": v(-56.3, 0.22) * mm, "end": v(-56.31, 0.26) * mm});
            skLineSegment(sketch, "E872", {"start": v(-56.31, 0.26) * mm, "end": v(-56.32, 0.28) * mm});
            skLineSegment(sketch, "E873", {"start": v(-56.32, 0.28) * mm, "end": v(-56.34, 0.3) * mm});
            skLineSegment(sketch, "E874", {"start": v(-56.34, 0.3) * mm, "end": v(-56.35, 0.31) * mm});
            skLineSegment(sketch, "E875", {"start": v(-56.35, 0.31) * mm, "end": v(-56.37, 0.33) * mm});
            skLineSegment(sketch, "E876", {"start": v(-56.37, 0.33) * mm, "end": v(-56.43, 0.35) * mm});
            skLineSegment(sketch, "E877", {"start": v(-56.43, 0.35) * mm, "end": v(-56.69, 0.39) * mm});
            skLineSegment(sketch, "E878", {"start": v(-56.69, 0.39) * mm, "end": v(-56.94, 0.44) * mm});
            skLineSegment(sketch, "E879", {"start": v(-56.94, 0.44) * mm, "end": v(-57, 0.44) * mm});
            skLineSegment(sketch, "E880", {"start": v(-57, 0.44) * mm, "end": v(-57.03, 0.43) * mm});
            skLineSegment(sketch, "E881", {"start": v(-57.03, 0.43) * mm, "end": v(-57.05, 0.42) * mm});
            skLineSegment(sketch, "E882", {"start": v(-57.05, 0.42) * mm, "end": v(-57.07, 0.4) * mm});
            skLineSegment(sketch, "E883", {"start": v(-57.07, 0.4) * mm, "end": v(-57.08, 0.4) * mm});
            skLineSegment(sketch, "E884", {"start": v(-57.08, 0.4) * mm, "end": v(-57.11, 0.37) * mm});
            skLineSegment(sketch, "E885", {"start": v(-57.11, 0.37) * mm, "end": v(-57.13, 0.34) * mm});
            skLineSegment(sketch, "E886", {"start": v(-57.13, 0.34) * mm, "end": v(-57.15, 0.3) * mm});
            skLineSegment(sketch, "E887", {"start": v(-57.15, 0.3) * mm, "end": v(-57.17, 0.27) * mm});
            skLineSegment(sketch, "E888", {"start": v(-57.17, 0.27) * mm, "end": v(-57.2, 0.2) * mm});
            skLineSegment(sketch, "E889", {"start": v(-57.2, 0.2) * mm, "end": v(-57.22, 0.14) * mm});
            skLineSegment(sketch, "E890", {"start": v(-57.22, 0.14) * mm, "end": v(-57.26, 0.08) * mm});
            skLineSegment(sketch, "E891", {"start": v(-57.26, 0.08) * mm, "end": v(-57.3, 0.02) * mm});
            skLineSegment(sketch, "E892", {"start": v(-57.3, 0.02) * mm, "end": v(-57.35, -0.04) * mm});
            skLineSegment(sketch, "E893", {"start": v(-57.35, -0.04) * mm, "end": v(-57.4, -0.1) * mm});
            skLineSegment(sketch, "E894", {"start": v(-57.4, -0.1) * mm, "end": v(-57.47, -0.14) * mm});
            skLineSegment(sketch, "E895", {"start": v(-57.47, -0.14) * mm, "end": v(-57.53, -0.2) * mm});
            skLineSegment(sketch, "E896", {"start": v(-57.53, -0.2) * mm, "end": v(-57.6, -0.24) * mm});
            skLineSegment(sketch, "E897", {"start": v(-57.6, -0.24) * mm, "end": v(-57.66, -0.3) * mm});
            skLineSegment(sketch, "E898", {"start": v(-57.66, -0.3) * mm, "end": v(-57.74, -0.34) * mm});
            skLineSegment(sketch, "E899", {"start": v(-57.74, -0.34) * mm, "end": v(-57.8, -0.37) * mm});
            skLineSegment(sketch, "E900", {"start": v(-57.8, -0.37) * mm, "end": v(-58.08, -0.22) * mm});
            skLineSegment(sketch, "E901", {"start": v(-58.08, -0.22) * mm, "end": v(-58.36, -0.05) * mm});
            skLineSegment(sketch, "E902", {"start": v(-58.36, -0.05) * mm, "end": v(-58.36, 0.02) * mm});
            skLineSegment(sketch, "E903", {"start": v(-58.36, 0.02) * mm, "end": v(-58.35, 0.1) * mm});
            skLineSegment(sketch, "E904", {"start": v(-58.35, 0.1) * mm, "end": v(-58.35, 0.2) * mm});
            skLineSegment(sketch, "E905", {"start": v(-58.35, 0.2) * mm, "end": v(-58.34, 0.27) * mm});
            skLineSegment(sketch, "E906", {"start": v(-58.34, 0.27) * mm, "end": v(-58.33, 0.35) * mm});
            skLineSegment(sketch, "E907", {"start": v(-58.33, 0.35) * mm, "end": v(-58.3, 0.43) * mm});
            skLineSegment(sketch, "E908", {"start": v(-58.3, 0.43) * mm, "end": v(-58.29, 0.5) * mm});
            skLineSegment(sketch, "E909", {"start": v(-58.29, 0.5) * mm, "end": v(-58.26, 0.58) * mm});
            skLineSegment(sketch, "E910", {"start": v(-58.26, 0.58) * mm, "end": v(-58.23, 0.64) * mm});
            skLineSegment(sketch, "E911", {"start": v(-58.23, 0.64) * mm, "end": v(-58.2, 0.7) * mm});
            skLineSegment(sketch, "E912", {"start": v(-58.2, 0.7) * mm, "end": v(-58.15, 0.76) * mm});
            skLineSegment(sketch, "E913", {"start": v(-58.15, 0.76) * mm, "end": v(-58.11, 0.82) * mm});
            skLineSegment(sketch, "E914", {"start": v(-58.11, 0.82) * mm, "end": v(-58.1, 0.85) * mm});
            skLineSegment(sketch, "E915", {"start": v(-58.1, 0.85) * mm, "end": v(-58.07, 0.88) * mm});
            skLineSegment(sketch, "E916", {"start": v(-58.07, 0.88) * mm, "end": v(-58.06, 0.92) * mm});
            skLineSegment(sketch, "E917", {"start": v(-58.06, 0.92) * mm, "end": v(-58.05, 0.95) * mm});
            skLineSegment(sketch, "E918", {"start": v(-58.05, 0.95) * mm, "end": v(-58.04, 0.97) * mm});
            skLineSegment(sketch, "E919", {"start": v(-58.04, 0.97) * mm, "end": v(-58.04, 1) * mm});
            skLineSegment(sketch, "E920", {"start": v(-58.04, 1) * mm, "end": v(-58.04, 1.02) * mm});
            skLineSegment(sketch, "E921", {"start": v(-58.04, 1.02) * mm, "end": v(-58.05, 1.05) * mm});
            skLineSegment(sketch, "E922", {"start": v(-58.05, 1.05) * mm, "end": v(-58.08, 1.1) * mm});
            skLineSegment(sketch, "E923", {"start": v(-58.08, 1.1) * mm, "end": v(-58.25, 1.3) * mm});
            skLineSegment(sketch, "E924", {"start": v(-58.25, 1.3) * mm, "end": v(-58.41, 1.5) * mm});
            skLineSegment(sketch, "E925", {"start": v(-58.41, 1.5) * mm, "end": v(-58.46, 1.54) * mm});
            skLineSegment(sketch, "E926", {"start": v(-58.46, 1.54) * mm, "end": v(-58.49, 1.55) * mm});
            skLineSegment(sketch, "E927", {"start": v(-58.49, 1.55) * mm, "end": v(-58.5, 1.55) * mm});
            skLineSegment(sketch, "E928", {"start": v(-58.5, 1.55) * mm, "end": v(-58.53, 1.55) * mm});
            skLineSegment(sketch, "E929", {"start": v(-58.53, 1.55) * mm, "end": v(-58.55, 1.55) * mm});
            skLineSegment(sketch, "E930", {"start": v(-58.55, 1.55) * mm, "end": v(-58.6, 1.55) * mm});
            skLineSegment(sketch, "E931", {"start": v(-58.6, 1.55) * mm, "end": v(-58.63, 1.54) * mm});
            skLineSegment(sketch, "E932", {"start": v(-58.63, 1.54) * mm, "end": v(-58.66, 1.53) * mm});
            skLineSegment(sketch, "E933", {"start": v(-58.66, 1.53) * mm, "end": v(-58.7, 1.51) * mm});
            skLineSegment(sketch, "E934", {"start": v(-58.7, 1.51) * mm, "end": v(-58.76, 1.48) * mm});
            skLineSegment(sketch, "E935", {"start": v(-58.76, 1.48) * mm, "end": v(-58.82, 1.45) * mm});
            skLineSegment(sketch, "E936", {"start": v(-58.82, 1.45) * mm, "end": v(-58.89, 1.42) * mm});
            skLineSegment(sketch, "E937", {"start": v(-58.89, 1.42) * mm, "end": v(-58.96, 1.4) * mm});
            skLineSegment(sketch, "E938", {"start": v(-58.96, 1.4) * mm, "end": v(-59.04, 1.4) * mm});
            skLineSegment(sketch, "E939", {"start": v(-59.04, 1.4) * mm, "end": v(-59.11, 1.39) * mm});
            skLineSegment(sketch, "E940", {"start": v(-59.11, 1.39) * mm, "end": v(-59.2, 1.38) * mm});
            skLineSegment(sketch, "E941", {"start": v(-59.2, 1.38) * mm, "end": v(-59.27, 1.38) * mm});
            skLineSegment(sketch, "E942", {"start": v(-59.27, 1.38) * mm, "end": v(-59.36, 1.39) * mm});
            skLineSegment(sketch, "E943", {"start": v(-59.36, 1.39) * mm, "end": v(-59.44, 1.4) * mm});
            skLineSegment(sketch, "E944", {"start": v(-59.44, 1.4) * mm, "end": v(-59.52, 1.41) * mm});
            skLineSegment(sketch, "E945", {"start": v(-59.52, 1.41) * mm, "end": v(-59.59, 1.42) * mm});
            skLineSegment(sketch, "E946", {"start": v(-59.59, 1.42) * mm, "end": v(-59.71, 1.72) * mm});
            skLineSegment(sketch, "E947", {"start": v(-59.71, 1.72) * mm, "end": v(-59.81, 2.03) * mm});
            skLineSegment(sketch, "E948", {"start": v(-59.81, 2.03) * mm, "end": v(-59.77, 2.08) * mm});
            skLineSegment(sketch, "E949", {"start": v(-59.77, 2.08) * mm, "end": v(-59.71, 2.15) * mm});
            skLineSegment(sketch, "E950", {"start": v(-59.71, 2.15) * mm, "end": v(-59.65, 2.2) * mm});
            skLineSegment(sketch, "E951", {"start": v(-59.65, 2.2) * mm, "end": v(-59.6, 2.26) * mm});
            skLineSegment(sketch, "E952", {"start": v(-59.6, 2.26) * mm, "end": v(-59.53, 2.32) * mm});
            skLineSegment(sketch, "E953", {"start": v(-59.53, 2.32) * mm, "end": v(-59.47, 2.37) * mm});
            skLineSegment(sketch, "E954", {"start": v(-59.47, 2.37) * mm, "end": v(-59.4, 2.4) * mm});
            skLineSegment(sketch, "E955", {"start": v(-59.4, 2.4) * mm, "end": v(-59.34, 2.45) * mm});
            skLineSegment(sketch, "E956", {"start": v(-59.34, 2.45) * mm, "end": v(-59.27, 2.48) * mm});
            skLineSegment(sketch, "E957", {"start": v(-59.27, 2.48) * mm, "end": v(-59.2, 2.5) * mm});
            skLineSegment(sketch, "E958", {"start": v(-59.2, 2.5) * mm, "end": v(-59.14, 2.52) * mm});
            skLineSegment(sketch, "E959", {"start": v(-59.14, 2.52) * mm, "end": v(-59.07, 2.54) * mm});
            skLineSegment(sketch, "E960", {"start": v(-59.07, 2.54) * mm, "end": v(-59.03, 2.55) * mm});
            skLineSegment(sketch, "E961", {"start": v(-59.03, 2.55) * mm, "end": v(-59, 2.56) * mm});
            skLineSegment(sketch, "E962", {"start": v(-59, 2.56) * mm, "end": v(-58.97, 2.58) * mm});
            skLineSegment(sketch, "E963", {"start": v(-58.97, 2.58) * mm, "end": v(-58.93, 2.6) * mm});
            skLineSegment(sketch, "E964", {"start": v(-58.93, 2.6) * mm, "end": v(-58.92, 2.61) * mm});
            skLineSegment(sketch, "E965", {"start": v(-58.92, 2.61) * mm, "end": v(-58.9, 2.63) * mm});
            skLineSegment(sketch, "E966", {"start": v(-58.9, 2.63) * mm, "end": v(-58.89, 2.65) * mm});
            skLineSegment(sketch, "E967", {"start": v(-58.89, 2.65) * mm, "end": v(-58.87, 2.67) * mm});
            skLineSegment(sketch, "E968", {"start": v(-58.87, 2.67) * mm, "end": v(-58.86, 2.73) * mm});
            skLineSegment(sketch, "E969", {"start": v(-58.86, 2.73) * mm, "end": v(-58.87, 3) * mm});
            skLineSegment(sketch, "E970", {"start": v(-58.87, 3) * mm, "end": v(-58.86, 3.25) * mm});
            skCircle(sketch, "E971", {"center": v(-56.23, 3) * mm, "radius": 1.59 * mm});
            skSolve(sketch);
        }
        {
            var Q0;
            Q0=makeQuery(id+"F7.imprint","IMPRINT",FACE,{"disambiguationData":[TD([[makeQuery(id+"F7.imprint","IMPRINT",EDGE,{"derivedFrom":sQuery(id+"F7.wireOp",EDGE,"E16")}),-1.0]])]});
            var Q1;
            Q1=makeQuery(id+"F7.imprint","IMPRINT",FACE,{"disambiguationData":[TD([[makeQuery(id+"F7.imprint","IMPRINT",EDGE,{"derivedFrom":sQuery(id+"F7.wireOp",EDGE,"E556")}),-1.0]])]});
            extrude(context, id + "F8", {"entities" : qUnion([Q0, Q1]), "depth" : 2.54 * mm, "offsetDistance" : 25.4 * mm});
        }
        {
            var Q0;
            Q0=makeQuery(id+"F8.opExtrude","CAP_FACE",FACE,{"disambiguationData":[OSD([sQuery(id+"F7.wireOp",EDGE,"E16"),sQuery(id+"F7.wireOp",EDGE,"E17"),sQuery(id+"F7.wireOp",EDGE,"E18"),sQuery(id+"F7.wireOp",EDGE,"E19"),sQuery(id+"F7.wireOp",EDGE,"E20"),sQuery(id+"F7.wireOp",EDGE,"E21"),sQuery(id+"F7.wireOp",EDGE,"E22"),sQuery(id+"F7.wireOp",EDGE,"E23"),sQuery(id+"F7.wireOp",EDGE,"E24"),sQuery(id+"F7.wireOp",EDGE,"E25"),sQuery(id+"F7.wireOp",EDGE,"E26"),sQuery(id+"F7.wireOp",EDGE,"E27"),sQuery(id+"F7.wireOp",EDGE,"E28"),sQuery(id+"F7.wireOp",EDGE,"E29"),sQuery(id+"F7.wireOp",EDGE,"E30"),sQuery(id+"F7.wireOp",EDGE,"E31"),sQuery(id+"F7.wireOp",EDGE,"E32"),sQuery(id+"F7.wireOp",EDGE,"E33"),sQuery(id+"F7.wireOp",EDGE,"E34"),sQuery(id+"F7.wireOp",EDGE,"E35"),sQuery(id+"F7.wireOp",EDGE,"E36"),sQuery(id+"F7.wireOp",EDGE,"E37"),sQuery(id+"F7.wireOp",EDGE,"E38"),sQuery(id+"F7.wireOp",EDGE,"E39"),sQuery(id+"F7.wireOp",EDGE,"E40"),sQuery(id+"F7.wireOp",EDGE,"E41"),sQuery(id+"F7.wireOp",EDGE,"E42"),sQuery(id+"F7.wireOp",EDGE,"E43"),sQuery(id+"F7.wireOp",EDGE,"E44"),sQuery(id+"F7.wireOp",EDGE,"E45"),sQuery(id+"F7.wireOp",EDGE,"E46"),sQuery(id+"F7.wireOp",EDGE,"E47"),sQuery(id+"F7.wireOp",EDGE,"E48"),sQuery(id+"F7.wireOp",EDGE,"E49"),sQuery(id+"F7.wireOp",EDGE,"E50"),sQuery(id+"F7.wireOp",EDGE,"E51"),sQuery(id+"F7.wireOp",EDGE,"E52"),sQuery(id+"F7.wireOp",EDGE,"E53"),sQuery(id+"F7.wireOp",EDGE,"E54"),sQuery(id+"F7.wireOp",EDGE,"E55"),sQuery(id+"F7.wireOp",EDGE,"E56"),sQuery(id+"F7.wireOp",EDGE,"E57"),sQuery(id+"F7.wireOp",EDGE,"E58"),sQuery(id+"F7.wireOp",EDGE,"E59"),sQuery(id+"F7.wireOp",EDGE,"E60"),sQuery(id+"F7.wireOp",EDGE,"E61"),sQuery(id+"F7.wireOp",EDGE,"E62"),sQuery(id+"F7.wireOp",EDGE,"E63"),sQuery(id+"F7.wireOp",EDGE,"E64"),sQuery(id+"F7.wireOp",EDGE,"E65"),sQuery(id+"F7.wireOp",EDGE,"E66"),sQuery(id+"F7.wireOp",EDGE,"E67"),sQuery(id+"F7.wireOp",EDGE,"E68"),sQuery(id+"F7.wireOp",EDGE,"E69"),sQuery(id+"F7.wireOp",EDGE,"E70"),sQuery(id+"F7.wireOp",EDGE,"E71"),sQuery(id+"F7.wireOp",EDGE,"E72"),sQuery(id+"F7.wireOp",EDGE,"E73"),sQuery(id+"F7.wireOp",EDGE,"E74"),sQuery(id+"F7.wireOp",EDGE,"E75"),sQuery(id+"F7.wireOp",EDGE,"E76"),sQuery(id+"F7.wireOp",EDGE,"E77"),sQuery(id+"F7.wireOp",EDGE,"E78"),sQuery(id+"F7.wireOp",EDGE,"E79"),sQuery(id+"F7.wireOp",EDGE,"E80"),sQuery(id+"F7.wireOp",EDGE,"E81"),sQuery(id+"F7.wireOp",EDGE,"E82"),sQuery(id+"F7.wireOp",EDGE,"E83"),sQuery(id+"F7.wireOp",EDGE,"E84"),sQuery(id+"F7.wireOp",EDGE,"E85"),sQuery(id+"F7.wireOp",EDGE,"E86"),sQuery(id+"F7.wireOp",EDGE,"E87"),sQuery(id+"F7.wireOp",EDGE,"E88"),sQuery(id+"F7.wireOp",EDGE,"E89"),sQuery(id+"F7.wireOp",EDGE,"E90"),sQuery(id+"F7.wireOp",EDGE,"E91"),sQuery(id+"F7.wireOp",EDGE,"E92"),sQuery(id+"F7.wireOp",EDGE,"E93"),sQuery(id+"F7.wireOp",EDGE,"E94"),sQuery(id+"F7.wireOp",EDGE,"E95"),sQuery(id+"F7.wireOp",EDGE,"E96"),sQuery(id+"F7.wireOp",EDGE,"E97"),sQuery(id+"F7.wireOp",EDGE,"E98"),sQuery(id+"F7.wireOp",EDGE,"E99"),sQuery(id+"F7.wireOp",EDGE,"E100"),sQuery(id+"F7.wireOp",EDGE,"E101"),sQuery(id+"F7.wireOp",EDGE,"E102"),sQuery(id+"F7.wireOp",EDGE,"E103"),sQuery(id+"F7.wireOp",EDGE,"E104"),sQuery(id+"F7.wireOp",EDGE,"E105"),sQuery(id+"F7.wireOp",EDGE,"E106"),sQuery(id+"F7.wireOp",EDGE,"E107"),sQuery(id+"F7.wireOp",EDGE,"E108"),sQuery(id+"F7.wireOp",EDGE,"E109"),sQuery(id+"F7.wireOp",EDGE,"E110"),sQuery(id+"F7.wireOp",EDGE,"E111"),sQuery(id+"F7.wireOp",EDGE,"E112"),sQuery(id+"F7.wireOp",EDGE,"E113"),sQuery(id+"F7.wireOp",EDGE,"E114"),sQuery(id+"F7.wireOp",EDGE,"E115"),sQuery(id+"F7.wireOp",EDGE,"E116"),sQuery(id+"F7.wireOp",EDGE,"E117"),sQuery(id+"F7.wireOp",EDGE,"E118"),sQuery(id+"F7.wireOp",EDGE,"E119"),sQuery(id+"F7.wireOp",EDGE,"E120"),sQuery(id+"F7.wireOp",EDGE,"E121"),sQuery(id+"F7.wireOp",EDGE,"E122"),sQuery(id+"F7.wireOp",EDGE,"E123"),sQuery(id+"F7.wireOp",EDGE,"E124"),sQuery(id+"F7.wireOp",EDGE,"E125"),sQuery(id+"F7.wireOp",EDGE,"E126"),sQuery(id+"F7.wireOp",EDGE,"E127"),sQuery(id+"F7.wireOp",EDGE,"E128"),sQuery(id+"F7.wireOp",EDGE,"E129"),sQuery(id+"F7.wireOp",EDGE,"E130"),sQuery(id+"F7.wireOp",EDGE,"E131"),sQuery(id+"F7.wireOp",EDGE,"E132"),sQuery(id+"F7.wireOp",EDGE,"E133"),sQuery(id+"F7.wireOp",EDGE,"E134"),sQuery(id+"F7.wireOp",EDGE,"E135"),sQuery(id+"F7.wireOp",EDGE,"E136"),sQuery(id+"F7.wireOp",EDGE,"E137"),sQuery(id+"F7.wireOp",EDGE,"E138"),sQuery(id+"F7.wireOp",EDGE,"E139"),sQuery(id+"F7.wireOp",EDGE,"E140"),sQuery(id+"F7.wireOp",EDGE,"E141"),sQuery(id+"F7.wireOp",EDGE,"E142"),sQuery(id+"F7.wireOp",EDGE,"E143"),sQuery(id+"F7.wireOp",EDGE,"E144"),sQuery(id+"F7.wireOp",EDGE,"E145"),sQuery(id+"F7.wireOp",EDGE,"E146"),sQuery(id+"F7.wireOp",EDGE,"E147"),sQuery(id+"F7.wireOp",EDGE,"E148"),sQuery(id+"F7.wireOp",EDGE,"E149"),sQuery(id+"F7.wireOp",EDGE,"E150"),sQuery(id+"F7.wireOp",EDGE,"E151"),sQuery(id+"F7.wireOp",EDGE,"E152"),sQuery(id+"F7.wireOp",EDGE,"E153"),sQuery(id+"F7.wireOp",EDGE,"E154"),sQuery(id+"F7.wireOp",EDGE,"E155"),sQuery(id+"F7.wireOp",EDGE,"E156"),sQuery(id+"F7.wireOp",EDGE,"E157"),sQuery(id+"F7.wireOp",EDGE,"E158"),sQuery(id+"F7.wireOp",EDGE,"E159"),sQuery(id+"F7.wireOp",EDGE,"E160"),sQuery(id+"F7.wireOp",EDGE,"E161"),sQuery(id+"F7.wireOp",EDGE,"E162"),sQuery(id+"F7.wireOp",EDGE,"E163"),sQuery(id+"F7.wireOp",EDGE,"E164"),sQuery(id+"F7.wireOp",EDGE,"E165"),sQuery(id+"F7.wireOp",EDGE,"E166"),sQuery(id+"F7.wireOp",EDGE,"E167"),sQuery(id+"F7.wireOp",EDGE,"E168"),sQuery(id+"F7.wireOp",EDGE,"E169"),sQuery(id+"F7.wireOp",EDGE,"E170"),sQuery(id+"F7.wireOp",EDGE,"E171"),sQuery(id+"F7.wireOp",EDGE,"E172"),sQuery(id+"F7.wireOp",EDGE,"E173"),sQuery(id+"F7.wireOp",EDGE,"E174"),sQuery(id+"F7.wireOp",EDGE,"E175"),sQuery(id+"F7.wireOp",EDGE,"E176"),sQuery(id+"F7.wireOp",EDGE,"E177"),sQuery(id+"F7.wireOp",EDGE,"E178"),sQuery(id+"F7.wireOp",EDGE,"E179"),sQuery(id+"F7.wireOp",EDGE,"E180"),sQuery(id+"F7.wireOp",EDGE,"E181"),sQuery(id+"F7.wireOp",EDGE,"E182"),sQuery(id+"F7.wireOp",EDGE,"E183"),sQuery(id+"F7.wireOp",EDGE,"E184"),sQuery(id+"F7.wireOp",EDGE,"E185"),sQuery(id+"F7.wireOp",EDGE,"E186"),sQuery(id+"F7.wireOp",EDGE,"E187"),sQuery(id+"F7.wireOp",EDGE,"E188"),sQuery(id+"F7.wireOp",EDGE,"E189"),sQuery(id+"F7.wireOp",EDGE,"E190"),sQuery(id+"F7.wireOp",EDGE,"E191"),sQuery(id+"F7.wireOp",EDGE,"E192"),sQuery(id+"F7.wireOp",EDGE,"E193"),sQuery(id+"F7.wireOp",EDGE,"E194"),sQuery(id+"F7.wireOp",EDGE,"E195"),sQuery(id+"F7.wireOp",EDGE,"E196"),sQuery(id+"F7.wireOp",EDGE,"E197"),sQuery(id+"F7.wireOp",EDGE,"E198"),sQuery(id+"F7.wireOp",EDGE,"E199"),sQuery(id+"F7.wireOp",EDGE,"E200"),sQuery(id+"F7.wireOp",EDGE,"E201"),sQuery(id+"F7.wireOp",EDGE,"E202"),sQuery(id+"F7.wireOp",EDGE,"E203"),sQuery(id+"F7.wireOp",EDGE,"E204"),sQuery(id+"F7.wireOp",EDGE,"E205"),sQuery(id+"F7.wireOp",EDGE,"E206"),sQuery(id+"F7.wireOp",EDGE,"E207"),sQuery(id+"F7.wireOp",EDGE,"E208"),sQuery(id+"F7.wireOp",EDGE,"E209"),sQuery(id+"F7.wireOp",EDGE,"E210"),sQuery(id+"F7.wireOp",EDGE,"E211"),sQuery(id+"F7.wireOp",EDGE,"E212"),sQuery(id+"F7.wireOp",EDGE,"E213"),sQuery(id+"F7.wireOp",EDGE,"E214"),sQuery(id+"F7.wireOp",EDGE,"E215"),sQuery(id+"F7.wireOp",EDGE,"E216"),sQuery(id+"F7.wireOp",EDGE,"E217"),sQuery(id+"F7.wireOp",EDGE,"E218"),sQuery(id+"F7.wireOp",EDGE,"E219"),sQuery(id+"F7.wireOp",EDGE,"E220"),sQuery(id+"F7.wireOp",EDGE,"E221"),sQuery(id+"F7.wireOp",EDGE,"E222"),sQuery(id+"F7.wireOp",EDGE,"E223"),sQuery(id+"F7.wireOp",EDGE,"E224"),sQuery(id+"F7.wireOp",EDGE,"E225"),sQuery(id+"F7.wireOp",EDGE,"E226"),sQuery(id+"F7.wireOp",EDGE,"E227"),sQuery(id+"F7.wireOp",EDGE,"E228"),sQuery(id+"F7.wireOp",EDGE,"E229"),sQuery(id+"F7.wireOp",EDGE,"E230"),sQuery(id+"F7.wireOp",EDGE,"E231"),sQuery(id+"F7.wireOp",EDGE,"E232"),sQuery(id+"F7.wireOp",EDGE,"E233"),sQuery(id+"F7.wireOp",EDGE,"E234"),sQuery(id+"F7.wireOp",EDGE,"E235"),sQuery(id+"F7.wireOp",EDGE,"E236"),sQuery(id+"F7.wireOp",EDGE,"E237"),sQuery(id+"F7.wireOp",EDGE,"E238"),sQuery(id+"F7.wireOp",EDGE,"E239"),sQuery(id+"F7.wireOp",EDGE,"E240"),sQuery(id+"F7.wireOp",EDGE,"E241"),sQuery(id+"F7.wireOp",EDGE,"E242"),sQuery(id+"F7.wireOp",EDGE,"E243"),sQuery(id+"F7.wireOp",EDGE,"E244"),sQuery(id+"F7.wireOp",EDGE,"E245"),sQuery(id+"F7.wireOp",EDGE,"E246"),sQuery(id+"F7.wireOp",EDGE,"E247"),sQuery(id+"F7.wireOp",EDGE,"E248"),sQuery(id+"F7.wireOp",EDGE,"E249"),sQuery(id+"F7.wireOp",EDGE,"E250"),sQuery(id+"F7.wireOp",EDGE,"E251"),sQuery(id+"F7.wireOp",EDGE,"E252"),sQuery(id+"F7.wireOp",EDGE,"E253"),sQuery(id+"F7.wireOp",EDGE,"E254"),sQuery(id+"F7.wireOp",EDGE,"E255"),sQuery(id+"F7.wireOp",EDGE,"E256"),sQuery(id+"F7.wireOp",EDGE,"E257"),sQuery(id+"F7.wireOp",EDGE,"E258"),sQuery(id+"F7.wireOp",EDGE,"E259"),sQuery(id+"F7.wireOp",EDGE,"E260"),sQuery(id+"F7.wireOp",EDGE,"E261"),sQuery(id+"F7.wireOp",EDGE,"E262"),sQuery(id+"F7.wireOp",EDGE,"E263"),sQuery(id+"F7.wireOp",EDGE,"E264"),sQuery(id+"F7.wireOp",EDGE,"E265"),sQuery(id+"F7.wireOp",EDGE,"E266"),sQuery(id+"F7.wireOp",EDGE,"E267"),sQuery(id+"F7.wireOp",EDGE,"E268"),sQuery(id+"F7.wireOp",EDGE,"E269"),sQuery(id+"F7.wireOp",EDGE,"E270"),sQuery(id+"F7.wireOp",EDGE,"E271"),sQuery(id+"F7.wireOp",EDGE,"E272"),sQuery(id+"F7.wireOp",EDGE,"E273"),sQuery(id+"F7.wireOp",EDGE,"E274"),sQuery(id+"F7.wireOp",EDGE,"E275"),sQuery(id+"F7.wireOp",EDGE,"E276"),sQuery(id+"F7.wireOp",EDGE,"E277"),sQuery(id+"F7.wireOp",EDGE,"E278"),sQuery(id+"F7.wireOp",EDGE,"E279"),sQuery(id+"F7.wireOp",EDGE,"E280"),sQuery(id+"F7.wireOp",EDGE,"E281"),sQuery(id+"F7.wireOp",EDGE,"E282"),sQuery(id+"F7.wireOp",EDGE,"E283"),sQuery(id+"F7.wireOp",EDGE,"E284"),sQuery(id+"F7.wireOp",EDGE,"E285"),sQuery(id+"F7.wireOp",EDGE,"E286"),sQuery(id+"F7.wireOp",EDGE,"E287"),sQuery(id+"F7.wireOp",EDGE,"E288"),sQuery(id+"F7.wireOp",EDGE,"E289"),sQuery(id+"F7.wireOp",EDGE,"E290"),sQuery(id+"F7.wireOp",EDGE,"E291"),sQuery(id+"F7.wireOp",EDGE,"E292"),sQuery(id+"F7.wireOp",EDGE,"E293"),sQuery(id+"F7.wireOp",EDGE,"E294"),sQuery(id+"F7.wireOp",EDGE,"E295"),sQuery(id+"F7.wireOp",EDGE,"E296"),sQuery(id+"F7.wireOp",EDGE,"E297"),sQuery(id+"F7.wireOp",EDGE,"E298"),sQuery(id+"F7.wireOp",EDGE,"E299"),sQuery(id+"F7.wireOp",EDGE,"E300"),sQuery(id+"F7.wireOp",EDGE,"E301"),sQuery(id+"F7.wireOp",EDGE,"E302"),sQuery(id+"F7.wireOp",EDGE,"E303"),sQuery(id+"F7.wireOp",EDGE,"E304"),sQuery(id+"F7.wireOp",EDGE,"E305"),sQuery(id+"F7.wireOp",EDGE,"E306"),sQuery(id+"F7.wireOp",EDGE,"E307"),sQuery(id+"F7.wireOp",EDGE,"E308"),sQuery(id+"F7.wireOp",EDGE,"E309"),sQuery(id+"F7.wireOp",EDGE,"E310"),sQuery(id+"F7.wireOp",EDGE,"E311"),sQuery(id+"F7.wireOp",EDGE,"E312"),sQuery(id+"F7.wireOp",EDGE,"E313"),sQuery(id+"F7.wireOp",EDGE,"E314"),sQuery(id+"F7.wireOp",EDGE,"E315"),sQuery(id+"F7.wireOp",EDGE,"E316"),sQuery(id+"F7.wireOp",EDGE,"E317"),sQuery(id+"F7.wireOp",EDGE,"E318"),sQuery(id+"F7.wireOp",EDGE,"E319"),sQuery(id+"F7.wireOp",EDGE,"E320"),sQuery(id+"F7.wireOp",EDGE,"E321"),sQuery(id+"F7.wireOp",EDGE,"E322"),sQuery(id+"F7.wireOp",EDGE,"E323"),sQuery(id+"F7.wireOp",EDGE,"E324"),sQuery(id+"F7.wireOp",EDGE,"E325"),sQuery(id+"F7.wireOp",EDGE,"E326"),sQuery(id+"F7.wireOp",EDGE,"E327"),sQuery(id+"F7.wireOp",EDGE,"E328"),sQuery(id+"F7.wireOp",EDGE,"E329"),sQuery(id+"F7.wireOp",EDGE,"E330"),sQuery(id+"F7.wireOp",EDGE,"E331"),sQuery(id+"F7.wireOp",EDGE,"E332"),sQuery(id+"F7.wireOp",EDGE,"E333"),sQuery(id+"F7.wireOp",EDGE,"E334"),sQuery(id+"F7.wireOp",EDGE,"E335"),sQuery(id+"F7.wireOp",EDGE,"E336"),sQuery(id+"F7.wireOp",EDGE,"E337"),sQuery(id+"F7.wireOp",EDGE,"E338"),sQuery(id+"F7.wireOp",EDGE,"E339"),sQuery(id+"F7.wireOp",EDGE,"E340"),sQuery(id+"F7.wireOp",EDGE,"E341"),sQuery(id+"F7.wireOp",EDGE,"E342"),sQuery(id+"F7.wireOp",EDGE,"E343"),sQuery(id+"F7.wireOp",EDGE,"E344"),sQuery(id+"F7.wireOp",EDGE,"E345"),sQuery(id+"F7.wireOp",EDGE,"E346"),sQuery(id+"F7.wireOp",EDGE,"E347"),sQuery(id+"F7.wireOp",EDGE,"E348"),sQuery(id+"F7.wireOp",EDGE,"E349"),sQuery(id+"F7.wireOp",EDGE,"E350"),sQuery(id+"F7.wireOp",EDGE,"E351"),sQuery(id+"F7.wireOp",EDGE,"E352"),sQuery(id+"F7.wireOp",EDGE,"E353"),sQuery(id+"F7.wireOp",EDGE,"E354"),sQuery(id+"F7.wireOp",EDGE,"E355"),sQuery(id+"F7.wireOp",EDGE,"E356"),sQuery(id+"F7.wireOp",EDGE,"E357"),sQuery(id+"F7.wireOp",EDGE,"E358"),sQuery(id+"F7.wireOp",EDGE,"E359"),sQuery(id+"F7.wireOp",EDGE,"E360"),sQuery(id+"F7.wireOp",EDGE,"E361"),sQuery(id+"F7.wireOp",EDGE,"E362"),sQuery(id+"F7.wireOp",EDGE,"E363"),sQuery(id+"F7.wireOp",EDGE,"E364"),sQuery(id+"F7.wireOp",EDGE,"E365"),sQuery(id+"F7.wireOp",EDGE,"E366"),sQuery(id+"F7.wireOp",EDGE,"E367"),sQuery(id+"F7.wireOp",EDGE,"E368"),sQuery(id+"F7.wireOp",EDGE,"E369"),sQuery(id+"F7.wireOp",EDGE,"E370"),sQuery(id+"F7.wireOp",EDGE,"E371"),sQuery(id+"F7.wireOp",EDGE,"E372"),sQuery(id+"F7.wireOp",EDGE,"E373"),sQuery(id+"F7.wireOp",EDGE,"E374"),sQuery(id+"F7.wireOp",EDGE,"E375"),sQuery(id+"F7.wireOp",EDGE,"E376"),sQuery(id+"F7.wireOp",EDGE,"E377"),sQuery(id+"F7.wireOp",EDGE,"E378"),sQuery(id+"F7.wireOp",EDGE,"E379"),sQuery(id+"F7.wireOp",EDGE,"E380"),sQuery(id+"F7.wireOp",EDGE,"E381"),sQuery(id+"F7.wireOp",EDGE,"E382"),sQuery(id+"F7.wireOp",EDGE,"E383"),sQuery(id+"F7.wireOp",EDGE,"E384"),sQuery(id+"F7.wireOp",EDGE,"E385"),sQuery(id+"F7.wireOp",EDGE,"E386"),sQuery(id+"F7.wireOp",EDGE,"E387"),sQuery(id+"F7.wireOp",EDGE,"E388"),sQuery(id+"F7.wireOp",EDGE,"E389"),sQuery(id+"F7.wireOp",EDGE,"E390"),sQuery(id+"F7.wireOp",EDGE,"E391"),sQuery(id+"F7.wireOp",EDGE,"E392"),sQuery(id+"F7.wireOp",EDGE,"E393"),sQuery(id+"F7.wireOp",EDGE,"E394"),sQuery(id+"F7.wireOp",EDGE,"E395"),sQuery(id+"F7.wireOp",EDGE,"E396"),sQuery(id+"F7.wireOp",EDGE,"E397"),sQuery(id+"F7.wireOp",EDGE,"E398"),sQuery(id+"F7.wireOp",EDGE,"E399"),sQuery(id+"F7.wireOp",EDGE,"E400"),sQuery(id+"F7.wireOp",EDGE,"E401"),sQuery(id+"F7.wireOp",EDGE,"E402"),sQuery(id+"F7.wireOp",EDGE,"E403"),sQuery(id+"F7.wireOp",EDGE,"E404"),sQuery(id+"F7.wireOp",EDGE,"E405"),sQuery(id+"F7.wireOp",EDGE,"E406"),sQuery(id+"F7.wireOp",EDGE,"E407"),sQuery(id+"F7.wireOp",EDGE,"E408"),sQuery(id+"F7.wireOp",EDGE,"E409"),sQuery(id+"F7.wireOp",EDGE,"E410"),sQuery(id+"F7.wireOp",EDGE,"E411"),sQuery(id+"F7.wireOp",EDGE,"E412"),sQuery(id+"F7.wireOp",EDGE,"E413"),sQuery(id+"F7.wireOp",EDGE,"E414"),sQuery(id+"F7.wireOp",EDGE,"E415"),sQuery(id+"F7.wireOp",EDGE,"E416"),sQuery(id+"F7.wireOp",EDGE,"E417"),sQuery(id+"F7.wireOp",EDGE,"E418"),sQuery(id+"F7.wireOp",EDGE,"E419"),sQuery(id+"F7.wireOp",EDGE,"E420"),sQuery(id+"F7.wireOp",EDGE,"E421"),sQuery(id+"F7.wireOp",EDGE,"E422"),sQuery(id+"F7.wireOp",EDGE,"E423"),sQuery(id+"F7.wireOp",EDGE,"E424"),sQuery(id+"F7.wireOp",EDGE,"E425"),sQuery(id+"F7.wireOp",EDGE,"E426"),sQuery(id+"F7.wireOp",EDGE,"E427"),sQuery(id+"F7.wireOp",EDGE,"E428"),sQuery(id+"F7.wireOp",EDGE,"E429"),sQuery(id+"F7.wireOp",EDGE,"E430"),sQuery(id+"F7.wireOp",EDGE,"E431"),sQuery(id+"F7.wireOp",EDGE,"E432"),sQuery(id+"F7.wireOp",EDGE,"E433"),sQuery(id+"F7.wireOp",EDGE,"E434"),sQuery(id+"F7.wireOp",EDGE,"E435"),sQuery(id+"F7.wireOp",EDGE,"E436"),sQuery(id+"F7.wireOp",EDGE,"E437"),sQuery(id+"F7.wireOp",EDGE,"E438"),sQuery(id+"F7.wireOp",EDGE,"E439"),sQuery(id+"F7.wireOp",EDGE,"E440"),sQuery(id+"F7.wireOp",EDGE,"E441"),sQuery(id+"F7.wireOp",EDGE,"E442"),sQuery(id+"F7.wireOp",EDGE,"E443"),sQuery(id+"F7.wireOp",EDGE,"E444"),sQuery(id+"F7.wireOp",EDGE,"E445"),sQuery(id+"F7.wireOp",EDGE,"E446"),sQuery(id+"F7.wireOp",EDGE,"E447"),sQuery(id+"F7.wireOp",EDGE,"E448"),sQuery(id+"F7.wireOp",EDGE,"E449"),sQuery(id+"F7.wireOp",EDGE,"E450"),sQuery(id+"F7.wireOp",EDGE,"E451"),sQuery(id+"F7.wireOp",EDGE,"E452"),sQuery(id+"F7.wireOp",EDGE,"E453"),sQuery(id+"F7.wireOp",EDGE,"E454"),sQuery(id+"F7.wireOp",EDGE,"E455"),sQuery(id+"F7.wireOp",EDGE,"E456"),sQuery(id+"F7.wireOp",EDGE,"E457"),sQuery(id+"F7.wireOp",EDGE,"E458"),sQuery(id+"F7.wireOp",EDGE,"E459"),sQuery(id+"F7.wireOp",EDGE,"E460"),sQuery(id+"F7.wireOp",EDGE,"E461"),sQuery(id+"F7.wireOp",EDGE,"E462"),sQuery(id+"F7.wireOp",EDGE,"E463"),sQuery(id+"F7.wireOp",EDGE,"E464"),sQuery(id+"F7.wireOp",EDGE,"E465"),sQuery(id+"F7.wireOp",EDGE,"E466"),sQuery(id+"F7.wireOp",EDGE,"E467"),sQuery(id+"F7.wireOp",EDGE,"E468"),sQuery(id+"F7.wireOp",EDGE,"E469"),sQuery(id+"F7.wireOp",EDGE,"E470"),sQuery(id+"F7.wireOp",EDGE,"E471"),sQuery(id+"F7.wireOp",EDGE,"E472"),sQuery(id+"F7.wireOp",EDGE,"E473"),sQuery(id+"F7.wireOp",EDGE,"E474"),sQuery(id+"F7.wireOp",EDGE,"E475"),sQuery(id+"F7.wireOp",EDGE,"E476"),sQuery(id+"F7.wireOp",EDGE,"E477"),sQuery(id+"F7.wireOp",EDGE,"E478"),sQuery(id+"F7.wireOp",EDGE,"E479"),sQuery(id+"F7.wireOp",EDGE,"E480"),sQuery(id+"F7.wireOp",EDGE,"E481"),sQuery(id+"F7.wireOp",EDGE,"E482"),sQuery(id+"F7.wireOp",EDGE,"E483"),sQuery(id+"F7.wireOp",EDGE,"E484"),sQuery(id+"F7.wireOp",EDGE,"E485"),sQuery(id+"F7.wireOp",EDGE,"E486"),sQuery(id+"F7.wireOp",EDGE,"E487"),sQuery(id+"F7.wireOp",EDGE,"E488"),sQuery(id+"F7.wireOp",EDGE,"E489"),sQuery(id+"F7.wireOp",EDGE,"E490"),sQuery(id+"F7.wireOp",EDGE,"E491"),sQuery(id+"F7.wireOp",EDGE,"E492"),sQuery(id+"F7.wireOp",EDGE,"E493"),sQuery(id+"F7.wireOp",EDGE,"E494"),sQuery(id+"F7.wireOp",EDGE,"E495"),sQuery(id+"F7.wireOp",EDGE,"E496"),sQuery(id+"F7.wireOp",EDGE,"E497"),sQuery(id+"F7.wireOp",EDGE,"E498"),sQuery(id+"F7.wireOp",EDGE,"E499"),sQuery(id+"F7.wireOp",EDGE,"E500"),sQuery(id+"F7.wireOp",EDGE,"E501"),sQuery(id+"F7.wireOp",EDGE,"E502"),sQuery(id+"F7.wireOp",EDGE,"E503"),sQuery(id+"F7.wireOp",EDGE,"E504"),sQuery(id+"F7.wireOp",EDGE,"E505"),sQuery(id+"F7.wireOp",EDGE,"E506"),sQuery(id+"F7.wireOp",EDGE,"E507"),sQuery(id+"F7.wireOp",EDGE,"E508"),sQuery(id+"F7.wireOp",EDGE,"E509"),sQuery(id+"F7.wireOp",EDGE,"E510"),sQuery(id+"F7.wireOp",EDGE,"E511"),sQuery(id+"F7.wireOp",EDGE,"E512"),sQuery(id+"F7.wireOp",EDGE,"E513"),sQuery(id+"F7.wireOp",EDGE,"E514"),sQuery(id+"F7.wireOp",EDGE,"E515"),sQuery(id+"F7.wireOp",EDGE,"E516"),sQuery(id+"F7.wireOp",EDGE,"E517"),sQuery(id+"F7.wireOp",EDGE,"E518"),sQuery(id+"F7.wireOp",EDGE,"E519"),sQuery(id+"F7.wireOp",EDGE,"E520"),sQuery(id+"F7.wireOp",EDGE,"E521"),sQuery(id+"F7.wireOp",EDGE,"E522"),sQuery(id+"F7.wireOp",EDGE,"E523"),sQuery(id+"F7.wireOp",EDGE,"E524"),sQuery(id+"F7.wireOp",EDGE,"E525"),sQuery(id+"F7.wireOp",EDGE,"E526"),sQuery(id+"F7.wireOp",EDGE,"E527"),sQuery(id+"F7.wireOp",EDGE,"E528"),sQuery(id+"F7.wireOp",EDGE,"E529"),sQuery(id+"F7.wireOp",EDGE,"E530"),sQuery(id+"F7.wireOp",EDGE,"E531"),sQuery(id+"F7.wireOp",EDGE,"E532"),sQuery(id+"F7.wireOp",EDGE,"E533"),sQuery(id+"F7.wireOp",EDGE,"E534"),sQuery(id+"F7.wireOp",EDGE,"E535"),sQuery(id+"F7.wireOp",EDGE,"E536"),sQuery(id+"F7.wireOp",EDGE,"E537"),sQuery(id+"F7.wireOp",EDGE,"E538"),sQuery(id+"F7.wireOp",EDGE,"E539"),sQuery(id+"F7.wireOp",EDGE,"E540"),sQuery(id+"F7.wireOp",EDGE,"E541"),sQuery(id+"F7.wireOp",EDGE,"E542"),sQuery(id+"F7.wireOp",EDGE,"E543"),sQuery(id+"F7.wireOp",EDGE,"E544"),sQuery(id+"F7.wireOp",EDGE,"E545"),sQuery(id+"F7.wireOp",EDGE,"E546"),sQuery(id+"F7.wireOp",EDGE,"E547"),sQuery(id+"F7.wireOp",EDGE,"E548"),sQuery(id+"F7.wireOp",EDGE,"E549"),sQuery(id+"F7.wireOp",EDGE,"E550"),sQuery(id+"F7.wireOp",EDGE,"E551"),sQuery(id+"F7.wireOp",EDGE,"E552"),sQuery(id+"F7.wireOp",EDGE,"E553"),sQuery(id+"F7.wireOp",EDGE,"E554"),sQuery(id+"F7.wireOp",EDGE,"E555"),sQuery(id+"F7.wireOp",EDGE,"E558"),sQuery(id+"F7.wireOp",EDGE,"E967")])],"isStart":false});
            extrude(context, id + "F9", {"entities" : qUnion([Q0]), "operationType" : NewBodyOperationType.ADD, "depth" : 1.27 * mm, "offsetDistance" : 25.4 * mm, "hasDraft" : true, "draftAngle" : 30 * degree, "draftPullDirection" : true});
        }
    });
